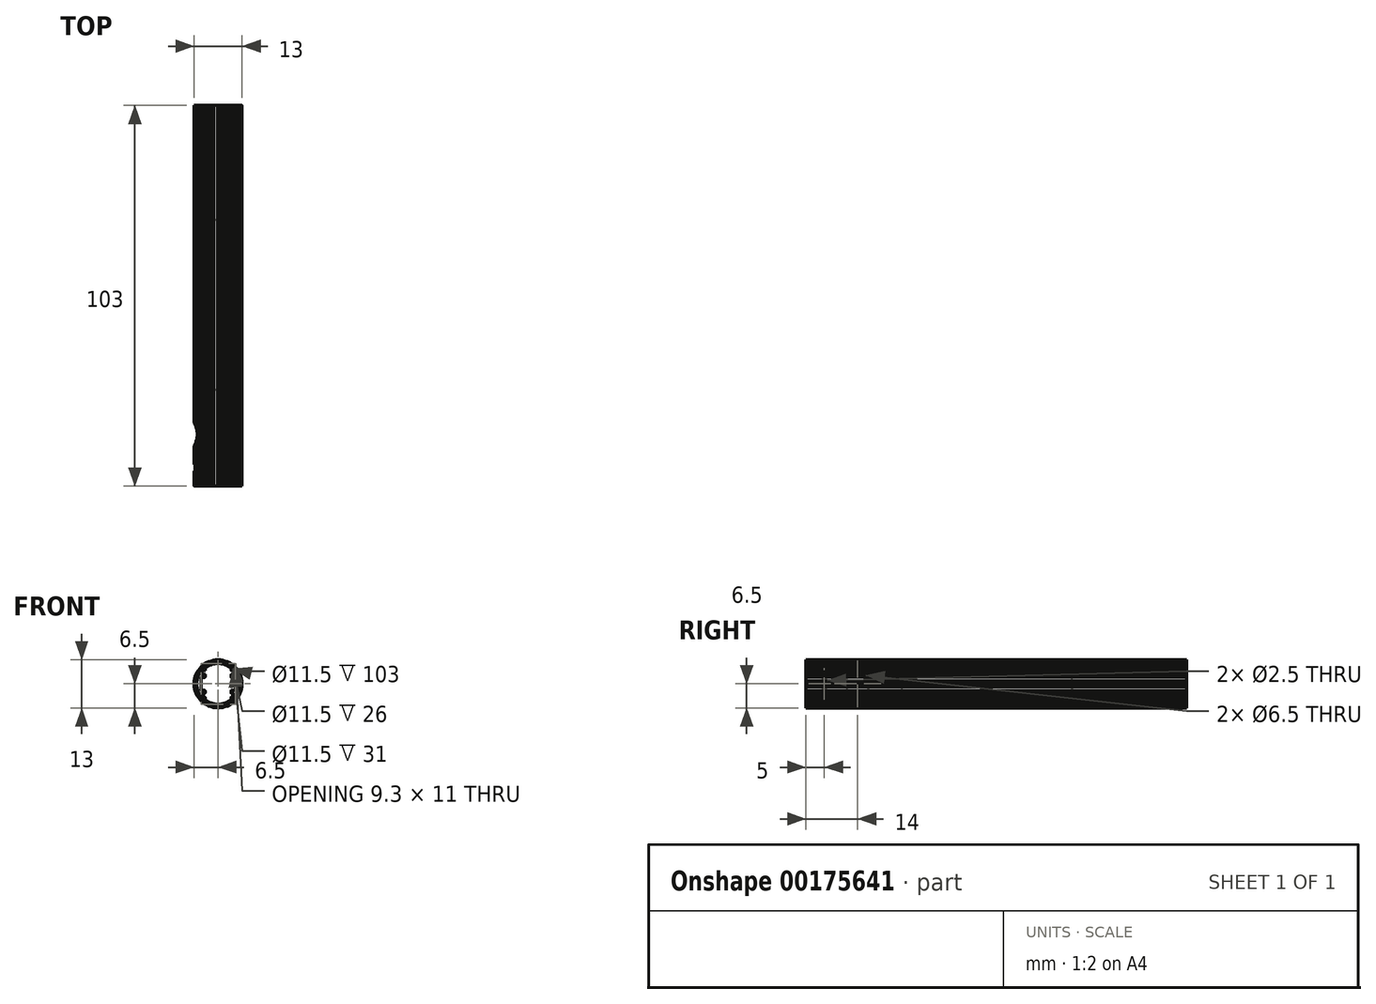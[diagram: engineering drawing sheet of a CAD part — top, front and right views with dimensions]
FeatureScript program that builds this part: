
annotation { "Feature Type Name" : "Feature", "Feature Type Description" : "" }
export const myFeature = defineFeature(function(context is Context, id is Id, definition is map)
    precondition{}
    {
        {
            assignVariable(context, id + "F0", {"name" : "Main_Length", "anyValue" : 103});
        }
        {
            assignVariable(context, id + "F1", {"name" : "Bore_Depth_F", "anyValue" : 26});
        }
        {
            assignVariable(context, id + "F2", {"name" : "Bore_Depth_R", "anyValue" : 31});
        }
        {
            var Q0;
            Q0=qCreatedBy(makeId("Front.planeOp"),FACE);
            var sketch = newSketch(context, id + "F3", { "sketchPlane" : qUnion([Q0])});
            skLineSegment(sketch, "E0", {"start": v(-3.5, -2.5) * mm, "end": v(-3.5, -1.85) * mm});
            skLineSegment(sketch, "E1", {"start": v(6.33, 0.97) * mm, "end": v(6.44, 0.88) * mm});
            skArc(sketch, "E2", {"start": v(-3.6, -1.75) * mm, "mid": v(-3.53, -1.78) * mm, "end": v(-3.5, -1.85) * mm});
            skArc(sketch, "E3", {"start": v(4.25, 3.55) * mm, "mid": v(4.32, 3.52) * mm, "end": v(4.35, 3.45) * mm});
            skArc(sketch, "E4", {"start": v(-3.5, -4.24) * mm, "mid": v(0, -5.5) * mm, "end": v(3.5, -4.24) * mm});
            skLineSegment(sketch, "E5", {"start": v(1.03, 6.32) * mm, "end": v(1.16, 6.4) * mm});
            skLineSegment(sketch, "E6", {"start": v(-4.95, -4.05) * mm, "end": v(-4.96, -4.2) * mm});
            skArc(sketch, "E7", {"start": v(-5.73, -3.08) * mm, "mid": v(-5.63, -3.25) * mm, "end": v(-5.53, -3.42) * mm});
            skLineSegment(sketch, "E8", {"start": v(3.51, 5.35) * mm, "end": v(3.66, 5.37) * mm});
            skLineSegment(sketch, "E9", {"start": v(4.65, -1.65) * mm, "end": v(4.65, 0) * mm});
            skLineSegment(sketch, "E10", {"start": v(-1.63, -6.19) * mm, "end": v(-1.55, -6.31) * mm});
            skArc(sketch, "E11", {"start": v(6.12, -2.2) * mm, "mid": v(6.18, -2) * mm, "end": v(6.24, -1.82) * mm});
            skArc(sketch, "E12", {"start": v(-2.83, -5.85) * mm, "mid": v(-2.64, -5.94) * mm, "end": v(-2.46, -6.02) * mm});
            skArc(sketch, "E13", {"start": v(2.83, 5.85) * mm, "mid": v(2.64, 5.94) * mm, "end": v(2.46, 6.02) * mm});
            skLineSegment(sketch, "E14", {"start": v(4.55, 4.5) * mm, "end": v(4.7, 4.5) * mm});
            skArc(sketch, "E15", {"start": v(-4.35, 2.7) * mm, "mid": v(-4.32, 2.63) * mm, "end": v(-4.25, 2.6) * mm});
            skArc(sketch, "E16", {"start": v(3.98, 5.14) * mm, "mid": v(3.82, 5.26) * mm, "end": v(3.66, 5.37) * mm});
            skLineSegment(sketch, "E17", {"start": v(-6.33, 0.97) * mm, "end": v(-6.44, 0.88) * mm});
            skArc(sketch, "E18", {"start": v(1.16, -6.4) * mm, "mid": v(1.35, -6.36) * mm, "end": v(1.55, -6.31) * mm});
            skLineSegment(sketch, "E19", {"start": v(-4, 5) * mm, "end": v(-3.98, 5.14) * mm});
            skArc(sketch, "E20", {"start": v(-1.55, -6.31) * mm, "mid": v(-1.35, -6.36) * mm, "end": v(-1.16, -6.4) * mm});
            skLineSegment(sketch, "E21", {"start": v(5.38, 3.46) * mm, "end": v(5.53, 3.42) * mm});
            skLineSegment(sketch, "E22", {"start": v(1.63, 6.19) * mm, "end": v(1.55, 6.31) * mm});
            skArc(sketch, "E23", {"start": v(3.5, -2.5) * mm, "mid": v(3.53, -2.57) * mm, "end": v(3.6, -2.6) * mm});
            skLineSegment(sketch, "E24", {"start": v(4, -5) * mm, "end": v(3.98, -5.14) * mm});
            skArc(sketch, "E25", {"start": v(3.6, 1.75) * mm, "mid": v(3.53, 1.78) * mm, "end": v(3.5, 1.85) * mm});
            skArc(sketch, "E26", {"start": v(2.88, -5.72) * mm, "mid": v(3.2, -5.54) * mm, "end": v(3.51, -5.35) * mm});
            skArc(sketch, "E27", {"start": v(-3.6, 3.55) * mm, "mid": v(-3.53, 3.58) * mm, "end": v(-3.5, 3.65) * mm});
            skArc(sketch, "E28", {"start": v(-5.53, 3.42) * mm, "mid": v(-5.63, 3.25) * mm, "end": v(-5.73, 3.08) * mm});
            skLineSegment(sketch, "E29", {"start": v(5.38, -3.46) * mm, "end": v(5.53, -3.42) * mm});
            skArc(sketch, "E30", {"start": v(5.73, 3.08) * mm, "mid": v(5.63, 3.25) * mm, "end": v(5.53, 3.42) * mm});
            skLineSegment(sketch, "E31", {"start": v(-4.25, 2.6) * mm, "end": v(-3.6, 2.6) * mm});
            skLineSegment(sketch, "E32", {"start": v(-3.5, 2.5) * mm, "end": v(-3.5, 1.85) * mm});
            skArc(sketch, "E33", {"start": v(6.24, 1.82) * mm, "mid": v(6.18, 2) * mm, "end": v(6.12, 2.2) * mm});
            skLineSegment(sketch, "E34", {"start": v(4.25, 2.6) * mm, "end": v(3.6, 2.6) * mm});
            skLineSegment(sketch, "E35", {"start": v(2.88, -5.72) * mm, "end": v(2.83, -5.85) * mm});
            skLineSegment(sketch, "E36", {"start": v(3.5, 4.24) * mm, "end": v(3.5, 3.65) * mm});
            skArc(sketch, "E37", {"start": v(5.99, 2.26) * mm, "mid": v(5.85, 2.6) * mm, "end": v(5.69, 2.93) * mm});
            skArc(sketch, "E38", {"start": v(0.3, -6.4) * mm, "mid": v(0.67, -6.36) * mm, "end": v(1.03, -6.32) * mm});
            skArc(sketch, "E39", {"start": v(6.48, 0.48) * mm, "mid": v(6.46, 0.68) * mm, "end": v(6.44, 0.88) * mm});
            skArc(sketch, "E40", {"start": v(-2.88, 5.72) * mm, "mid": v(-3.2, 5.54) * mm, "end": v(-3.51, 5.35) * mm});
            skLineSegment(sketch, "E41", {"start": v(-0.3, 6.4) * mm, "end": v(-0.2, 6.5) * mm});
            skLineSegment(sketch, "E42", {"start": v(5.69, 2.93) * mm, "end": v(5.73, 3.08) * mm});
            skLineSegment(sketch, "E43", {"start": v(1.63, -6.19) * mm, "end": v(1.55, -6.31) * mm});
            skArc(sketch, "E44", {"start": v(-0.3, 6.4) * mm, "mid": v(-0.67, 6.36) * mm, "end": v(-1.03, 6.32) * mm});
            skLineSegment(sketch, "E45", {"start": v(-3.51, 5.35) * mm, "end": v(-3.66, 5.37) * mm});
            skLineSegment(sketch, "E46", {"start": v(-1.63, 6.19) * mm, "end": v(-1.55, 6.31) * mm});
            skLineSegment(sketch, "E47", {"start": v(4.55, -4.5) * mm, "end": v(4.7, -4.5) * mm});
            skArc(sketch, "E48", {"start": v(6.44, -0.88) * mm, "mid": v(6.46, -0.68) * mm, "end": v(6.48, -0.48) * mm});
            skArc(sketch, "E49", {"start": v(-2.46, 6.02) * mm, "mid": v(-2.64, 5.94) * mm, "end": v(-2.83, 5.85) * mm});
            skArc(sketch, "E50", {"start": v(6.33, 0.97) * mm, "mid": v(6.26, 1.33) * mm, "end": v(6.17, 1.69) * mm});
            skArc(sketch, "E51", {"start": v(3.6, 3.55) * mm, "mid": v(3.53, 3.58) * mm, "end": v(3.5, 3.65) * mm});
            skLineSegment(sketch, "E52", {"start": v(3.5, 2.5) * mm, "end": v(3.5, 1.85) * mm});
            skArc(sketch, "E53", {"start": v(-0.2, -6.5) * mm, "mid": v(0, -6.5) * mm, "end": v(0.2, -6.5) * mm});
            skArc(sketch, "E54", {"start": v(4.96, 4.2) * mm, "mid": v(4.83, 4.35) * mm, "end": v(4.7, 4.5) * mm});
            skLineSegment(sketch, "E55", {"start": v(2.32, 5.96) * mm, "end": v(2.46, 6.02) * mm});
            skArc(sketch, "E56", {"start": v(4.35, 2.7) * mm, "mid": v(4.32, 2.63) * mm, "end": v(4.25, 2.6) * mm});
            skLineSegment(sketch, "E57", {"start": v(-4.65, -1.65) * mm, "end": v(-4.65, 0) * mm});
            skArc(sketch, "E58", {"start": v(-1.63, 6.19) * mm, "mid": v(-1.98, 6.09) * mm, "end": v(-2.32, 5.96) * mm});
            skLineSegment(sketch, "E59", {"start": v(-1.03, 6.32) * mm, "end": v(-1.16, 6.4) * mm});
            skLineSegment(sketch, "E60", {"start": v(0.3, -6.4) * mm, "end": v(0.2, -6.5) * mm});
            skArc(sketch, "E61", {"start": v(-4.7, 4.5) * mm, "mid": v(-4.83, 4.35) * mm, "end": v(-4.96, 4.2) * mm});
            skArc(sketch, "E62", {"start": v(-5.69, 2.93) * mm, "mid": v(-5.85, 2.6) * mm, "end": v(-5.99, 2.26) * mm});
            skArc(sketch, "E63", {"start": v(4.25, -3.55) * mm, "mid": v(4.32, -3.52) * mm, "end": v(4.35, -3.45) * mm});
            skLineSegment(sketch, "E64", {"start": v(-4.35, 3.45) * mm, "end": v(-4.35, 2.7) * mm});
            skLineSegment(sketch, "E65", {"start": v(-4.65, 1.65) * mm, "end": v(-4.65, 0) * mm});
            skArc(sketch, "E66", {"start": v(5.69, -2.93) * mm, "mid": v(5.85, -2.6) * mm, "end": v(5.99, -2.26) * mm});
            skArc(sketch, "E67", {"start": v(-4.55, 1.75) * mm, "mid": v(-4.62, 1.72) * mm, "end": v(-4.65, 1.65) * mm});
            skLineSegment(sketch, "E68", {"start": v(-3.5, 4.24) * mm, "end": v(-3.5, 3.65) * mm});
            skLineSegment(sketch, "E69", {"start": v(-3.6, 3.55) * mm, "end": v(-4.25, 3.55) * mm});
            skLineSegment(sketch, "E70", {"start": v(-3.6, 1.75) * mm, "end": v(-4.55, 1.75) * mm});
            skArc(sketch, "E71", {"start": v(-3.5, 2.5) * mm, "mid": v(-3.53, 2.57) * mm, "end": v(-3.6, 2.6) * mm});
            skArc(sketch, "E72", {"start": v(-3.6, 1.75) * mm, "mid": v(-3.53, 1.78) * mm, "end": v(-3.5, 1.85) * mm});
            skArc(sketch, "E73", {"start": v(-4.25, 3.55) * mm, "mid": v(-4.32, 3.52) * mm, "end": v(-4.35, 3.45) * mm});
            skArc(sketch, "E74", {"start": v(4.55, 1.75) * mm, "mid": v(4.62, 1.72) * mm, "end": v(4.65, 1.65) * mm});
            skLineSegment(sketch, "E75", {"start": v(3.6, 1.75) * mm, "end": v(4.55, 1.75) * mm});
            skArc(sketch, "E76", {"start": v(3.5, 2.5) * mm, "mid": v(3.53, 2.57) * mm, "end": v(3.6, 2.6) * mm});
            skArc(sketch, "E77", {"start": v(0.2, 6.5) * mm, "mid": v(0, 6.5) * mm, "end": v(-0.2, 6.5) * mm});
            skLineSegment(sketch, "E78", {"start": v(3.6, 3.55) * mm, "end": v(4.25, 3.55) * mm});
            skLineSegment(sketch, "E79", {"start": v(4.65, 1.65) * mm, "end": v(4.65, 0) * mm});
            skLineSegment(sketch, "E80", {"start": v(4.35, 3.45) * mm, "end": v(4.35, 2.7) * mm});
            skArc(sketch, "E81", {"start": v(-3.6, -3.55) * mm, "mid": v(-3.53, -3.58) * mm, "end": v(-3.5, -3.65) * mm});
            skLineSegment(sketch, "E82", {"start": v(-4.25, -2.6) * mm, "end": v(-3.6, -2.6) * mm});
            skLineSegment(sketch, "E83", {"start": v(-3.6, -1.75) * mm, "end": v(-4.55, -1.75) * mm});
            skArc(sketch, "E84", {"start": v(-3.5, -2.5) * mm, "mid": v(-3.53, -2.57) * mm, "end": v(-3.6, -2.6) * mm});
            skArc(sketch, "E85", {"start": v(-4.55, -1.75) * mm, "mid": v(-4.62, -1.72) * mm, "end": v(-4.65, -1.65) * mm});
            skArc(sketch, "E86", {"start": v(-4.35, -2.7) * mm, "mid": v(-4.32, -2.63) * mm, "end": v(-4.25, -2.6) * mm});
            skArc(sketch, "E87", {"start": v(-4.25, -3.55) * mm, "mid": v(-4.32, -3.52) * mm, "end": v(-4.35, -3.45) * mm});
            skArc(sketch, "E88", {"start": v(3.6, -1.75) * mm, "mid": v(3.53, -1.78) * mm, "end": v(3.5, -1.85) * mm});
            skLineSegment(sketch, "E89", {"start": v(-2.32, 5.96) * mm, "end": v(-2.46, 6.02) * mm});
            skArc(sketch, "E90", {"start": v(4.55, -1.75) * mm, "mid": v(4.62, -1.72) * mm, "end": v(4.65, -1.65) * mm});
            skLineSegment(sketch, "E91", {"start": v(3.6, -1.75) * mm, "end": v(4.55, -1.75) * mm});
            skArc(sketch, "E92", {"start": v(4.35, -2.7) * mm, "mid": v(4.32, -2.63) * mm, "end": v(4.25, -2.6) * mm});
            skLineSegment(sketch, "E93", {"start": v(4.25, -2.6) * mm, "end": v(3.6, -2.6) * mm});
            skArc(sketch, "E94", {"start": v(3.6, -3.55) * mm, "mid": v(3.53, -3.58) * mm, "end": v(3.5, -3.65) * mm});
            skLineSegment(sketch, "E95", {"start": v(-3.5, -4.24) * mm, "end": v(-3.5, -3.65) * mm});
            skLineSegment(sketch, "E96", {"start": v(3.5, -2.5) * mm, "end": v(3.5, -1.85) * mm});
            skLineSegment(sketch, "E97", {"start": v(4.35, -3.45) * mm, "end": v(4.35, -2.7) * mm});
            skLineSegment(sketch, "E98", {"start": v(-3.6, -3.55) * mm, "end": v(-4.25, -3.55) * mm});
            skArc(sketch, "E99", {"start": v(-6.12, 2.2) * mm, "mid": v(-6.18, 2) * mm, "end": v(-6.24, 1.82) * mm});
            skLineSegment(sketch, "E100", {"start": v(-4.35, -3.45) * mm, "end": v(-4.35, -2.7) * mm});
            skLineSegment(sketch, "E101", {"start": v(3.6, -3.55) * mm, "end": v(4.25, -3.55) * mm});
            skLineSegment(sketch, "E102", {"start": v(-5.38, 3.46) * mm, "end": v(-5.53, 3.42) * mm});
            skLineSegment(sketch, "E103", {"start": v(3.5, -4.24) * mm, "end": v(3.5, -3.65) * mm});
            skArc(sketch, "E104", {"start": v(3.5, 4.24) * mm, "mid": v(0, 5.5) * mm, "end": v(-3.5, 4.24) * mm});
            skLineSegment(sketch, "E105", {"start": v(-0.3, -6.4) * mm, "end": v(-0.2, -6.5) * mm});
            skArc(sketch, "E106", {"start": v(1.63, -6.19) * mm, "mid": v(1.98, -6.09) * mm, "end": v(2.32, -5.96) * mm});
            skLineSegment(sketch, "E107", {"start": v(1.03, -6.32) * mm, "end": v(1.16, -6.4) * mm});
            skArc(sketch, "E108", {"start": v(2.46, -6.02) * mm, "mid": v(2.64, -5.94) * mm, "end": v(2.83, -5.85) * mm});
            skArc(sketch, "E109", {"start": v(-6.24, -1.82) * mm, "mid": v(-6.18, -2) * mm, "end": v(-6.12, -2.2) * mm});
            skLineSegment(sketch, "E110", {"start": v(2.32, -5.96) * mm, "end": v(2.46, -6.02) * mm});
            skArc(sketch, "E111", {"start": v(4, -5) * mm, "mid": v(4.28, -4.76) * mm, "end": v(4.55, -4.5) * mm});
            skArc(sketch, "E112", {"start": v(3.66, -5.37) * mm, "mid": v(3.82, -5.26) * mm, "end": v(3.98, -5.14) * mm});
            skLineSegment(sketch, "E113", {"start": v(3.51, -5.35) * mm, "end": v(3.66, -5.37) * mm});
            skLineSegment(sketch, "E114", {"start": v(-3.51, -5.35) * mm, "end": v(-3.66, -5.37) * mm});
            skLineSegment(sketch, "E115", {"start": v(4.95, -4.05) * mm, "end": v(4.96, -4.2) * mm});
            skLineSegment(sketch, "E116", {"start": v(-4.55, -4.5) * mm, "end": v(-4.7, -4.5) * mm});
            skArc(sketch, "E117", {"start": v(5.53, -3.42) * mm, "mid": v(5.63, -3.25) * mm, "end": v(5.73, -3.08) * mm});
            skArc(sketch, "E118", {"start": v(4.7, -4.5) * mm, "mid": v(4.83, -4.35) * mm, "end": v(4.96, -4.2) * mm});
            skArc(sketch, "E119", {"start": v(-3.98, -5.14) * mm, "mid": v(-3.82, -5.26) * mm, "end": v(-3.66, -5.37) * mm});
            skArc(sketch, "E120", {"start": v(6.17, -1.69) * mm, "mid": v(6.26, -1.33) * mm, "end": v(6.33, -0.97) * mm});
            skLineSegment(sketch, "E121", {"start": v(6.17, -1.69) * mm, "end": v(6.24, -1.82) * mm});
            skLineSegment(sketch, "E122", {"start": v(5.99, -2.26) * mm, "end": v(6.12, -2.2) * mm});
            skArc(sketch, "E123", {"start": v(6.39, -0.37) * mm, "mid": v(6.4, 0) * mm, "end": v(6.39, 0.37) * mm});
            skLineSegment(sketch, "E124", {"start": v(6.39, -0.37) * mm, "end": v(6.48, -0.48) * mm});
            skLineSegment(sketch, "E125", {"start": v(-1.03, -6.32) * mm, "end": v(-1.16, -6.4) * mm});
            skLineSegment(sketch, "E126", {"start": v(6.33, -0.97) * mm, "end": v(6.44, -0.88) * mm});
            skLineSegment(sketch, "E127", {"start": v(5.99, 2.26) * mm, "end": v(6.12, 2.2) * mm});
            skLineSegment(sketch, "E128", {"start": v(6.17, 1.69) * mm, "end": v(6.24, 1.82) * mm});
            skArc(sketch, "E129", {"start": v(5.38, 3.46) * mm, "mid": v(5.18, 3.76) * mm, "end": v(4.95, 4.05) * mm});
            skArc(sketch, "E130", {"start": v(4.55, 4.5) * mm, "mid": v(4.28, 4.76) * mm, "end": v(4, 5) * mm});
            skLineSegment(sketch, "E131", {"start": v(4.95, 4.05) * mm, "end": v(4.96, 4.2) * mm});
            skArc(sketch, "E132", {"start": v(3.51, 5.35) * mm, "mid": v(3.2, 5.54) * mm, "end": v(2.88, 5.72) * mm});
            skLineSegment(sketch, "E133", {"start": v(4, 5) * mm, "end": v(3.98, 5.14) * mm});
            skArc(sketch, "E134", {"start": v(2.32, 5.96) * mm, "mid": v(1.98, 6.09) * mm, "end": v(1.63, 6.19) * mm});
            skLineSegment(sketch, "E135", {"start": v(2.88, 5.72) * mm, "end": v(2.83, 5.85) * mm});
            skArc(sketch, "E136", {"start": v(1.03, 6.32) * mm, "mid": v(0.67, 6.36) * mm, "end": v(0.3, 6.4) * mm});
            skArc(sketch, "E137", {"start": v(1.55, 6.31) * mm, "mid": v(1.35, 6.36) * mm, "end": v(1.16, 6.4) * mm});
            skLineSegment(sketch, "E138", {"start": v(0.3, 6.4) * mm, "end": v(0.2, 6.5) * mm});
            skArc(sketch, "E139", {"start": v(-1.16, 6.4) * mm, "mid": v(-1.35, 6.36) * mm, "end": v(-1.55, 6.31) * mm});
            skLineSegment(sketch, "E140", {"start": v(-2.88, 5.72) * mm, "end": v(-2.83, 5.85) * mm});
            skArc(sketch, "E141", {"start": v(-4, 5) * mm, "mid": v(-4.28, 4.76) * mm, "end": v(-4.55, 4.5) * mm});
            skArc(sketch, "E142", {"start": v(-3.66, 5.37) * mm, "mid": v(-3.82, 5.26) * mm, "end": v(-3.98, 5.14) * mm});
            skLineSegment(sketch, "E143", {"start": v(-6.33, -0.97) * mm, "end": v(-6.44, -0.88) * mm});
            skLineSegment(sketch, "E144", {"start": v(-4.95, 4.05) * mm, "end": v(-4.96, 4.2) * mm});
            skLineSegment(sketch, "E145", {"start": v(-4.55, 4.5) * mm, "end": v(-4.7, 4.5) * mm});
            skArc(sketch, "E146", {"start": v(-6.17, 1.69) * mm, "mid": v(-6.26, 1.33) * mm, "end": v(-6.33, 0.97) * mm});
            skLineSegment(sketch, "E147", {"start": v(-6.17, 1.69) * mm, "end": v(-6.24, 1.82) * mm});
            skLineSegment(sketch, "E148", {"start": v(-5.99, 2.26) * mm, "end": v(-6.12, 2.2) * mm});
            skArc(sketch, "E149", {"start": v(-6.39, 0.37) * mm, "mid": v(-6.4, 0) * mm, "end": v(-6.39, -0.37) * mm});
            skArc(sketch, "E150", {"start": v(-6.44, 0.88) * mm, "mid": v(-6.46, 0.68) * mm, "end": v(-6.48, 0.48) * mm});
            skLineSegment(sketch, "E151", {"start": v(-6.39, 0.37) * mm, "end": v(-6.48, 0.48) * mm});
            skLineSegment(sketch, "E152", {"start": v(5.69, -2.93) * mm, "end": v(5.73, -3.08) * mm});
            skArc(sketch, "E153", {"start": v(-6.33, -0.97) * mm, "mid": v(-6.26, -1.33) * mm, "end": v(-6.17, -1.69) * mm});
            skArc(sketch, "E154", {"start": v(-6.48, -0.48) * mm, "mid": v(-6.46, -0.68) * mm, "end": v(-6.44, -0.88) * mm});
            skLineSegment(sketch, "E155", {"start": v(-6.39, -0.37) * mm, "end": v(-6.48, -0.48) * mm});
            skArc(sketch, "E156", {"start": v(-5.99, -2.26) * mm, "mid": v(-5.85, -2.6) * mm, "end": v(-5.69, -2.93) * mm});
            skLineSegment(sketch, "E157", {"start": v(-5.99, -2.26) * mm, "end": v(-6.12, -2.2) * mm});
            skLineSegment(sketch, "E158", {"start": v(-6.17, -1.69) * mm, "end": v(-6.24, -1.82) * mm});
            skArc(sketch, "E159", {"start": v(-5.38, -3.46) * mm, "mid": v(-5.18, -3.76) * mm, "end": v(-4.95, -4.05) * mm});
            skLineSegment(sketch, "E160", {"start": v(-5.38, -3.46) * mm, "end": v(-5.53, -3.42) * mm});
            skLineSegment(sketch, "E161", {"start": v(-5.69, -2.93) * mm, "end": v(-5.73, -3.08) * mm});
            skArc(sketch, "E162", {"start": v(-4.55, -4.5) * mm, "mid": v(-4.28, -4.76) * mm, "end": v(-4, -5) * mm});
            skLineSegment(sketch, "E163", {"start": v(6.39, 0.37) * mm, "end": v(6.48, 0.48) * mm});
            skArc(sketch, "E164", {"start": v(-4.96, -4.2) * mm, "mid": v(-4.83, -4.35) * mm, "end": v(-4.7, -4.5) * mm});
            skArc(sketch, "E165", {"start": v(4.95, -4.05) * mm, "mid": v(5.18, -3.76) * mm, "end": v(5.38, -3.46) * mm});
            skLineSegment(sketch, "E166", {"start": v(-4, -5) * mm, "end": v(-3.98, -5.14) * mm});
            skArc(sketch, "E167", {"start": v(-2.32, -5.96) * mm, "mid": v(-1.98, -6.09) * mm, "end": v(-1.63, -6.19) * mm});
            skLineSegment(sketch, "E168", {"start": v(-2.32, -5.96) * mm, "end": v(-2.46, -6.02) * mm});
            skLineSegment(sketch, "E169", {"start": v(-2.88, -5.72) * mm, "end": v(-2.83, -5.85) * mm});
            skArc(sketch, "E170", {"start": v(-1.03, -6.32) * mm, "mid": v(-0.67, -6.36) * mm, "end": v(-0.3, -6.4) * mm});
            skArc(sketch, "E171", {"start": v(-4.95, 4.05) * mm, "mid": v(-5.18, 3.76) * mm, "end": v(-5.38, 3.46) * mm});
            skLineSegment(sketch, "E172", {"start": v(-5.69, 2.93) * mm, "end": v(-5.73, 3.08) * mm});
            skArc(sketch, "E173", {"start": v(-3.51, -5.35) * mm, "mid": v(-3.2, -5.54) * mm, "end": v(-2.88, -5.72) * mm});
            skSolve(sketch);
        }
        {
            var Q0;
            Q0=makeQuery(id+"F3.imprint","IMPRINT",FACE,{"disambiguationData":[TD([[makeQuery(id+"F3.imprint","IMPRINT",EDGE,{"derivedFrom":sQuery(id+"F3.wireOp",EDGE,"E0")}),1.0]])]});
            extrude(context, id + "F4", {"entities" : qUnion([Q0]), "depth" : (getVariable(context, 'Main_Length') - getVariable(context, 'Bore_Depth_F') - getVariable(context, 'Bore_Depth_R')) * mm});
        }
        {
            var Q0;
            Q0=makeQuery(id+"F4.opExtrude","CAP_FACE",FACE,{"disambiguationData":[OSD([sQuery(id+"F3.wireOp",EDGE,"E0"),sQuery(id+"F3.wireOp",EDGE,"E1"),sQuery(id+"F3.wireOp",EDGE,"E2"),sQuery(id+"F3.wireOp",EDGE,"E3"),sQuery(id+"F3.wireOp",EDGE,"E4"),sQuery(id+"F3.wireOp",EDGE,"E5"),sQuery(id+"F3.wireOp",EDGE,"E6"),sQuery(id+"F3.wireOp",EDGE,"E7"),sQuery(id+"F3.wireOp",EDGE,"E8"),sQuery(id+"F3.wireOp",EDGE,"E9"),sQuery(id+"F3.wireOp",EDGE,"E10"),sQuery(id+"F3.wireOp",EDGE,"E11"),sQuery(id+"F3.wireOp",EDGE,"E12"),sQuery(id+"F3.wireOp",EDGE,"E13"),sQuery(id+"F3.wireOp",EDGE,"E14"),sQuery(id+"F3.wireOp",EDGE,"E15"),sQuery(id+"F3.wireOp",EDGE,"E16"),sQuery(id+"F3.wireOp",EDGE,"E17"),sQuery(id+"F3.wireOp",EDGE,"E18"),sQuery(id+"F3.wireOp",EDGE,"E19"),sQuery(id+"F3.wireOp",EDGE,"E20"),sQuery(id+"F3.wireOp",EDGE,"E21"),sQuery(id+"F3.wireOp",EDGE,"E22"),sQuery(id+"F3.wireOp",EDGE,"E23"),sQuery(id+"F3.wireOp",EDGE,"E24"),sQuery(id+"F3.wireOp",EDGE,"E25"),sQuery(id+"F3.wireOp",EDGE,"E26"),sQuery(id+"F3.wireOp",EDGE,"E27"),sQuery(id+"F3.wireOp",EDGE,"E28"),sQuery(id+"F3.wireOp",EDGE,"E29"),sQuery(id+"F3.wireOp",EDGE,"E30"),sQuery(id+"F3.wireOp",EDGE,"E31"),sQuery(id+"F3.wireOp",EDGE,"E32"),sQuery(id+"F3.wireOp",EDGE,"E33"),sQuery(id+"F3.wireOp",EDGE,"E34"),sQuery(id+"F3.wireOp",EDGE,"E35"),sQuery(id+"F3.wireOp",EDGE,"E36"),sQuery(id+"F3.wireOp",EDGE,"E37"),sQuery(id+"F3.wireOp",EDGE,"E38"),sQuery(id+"F3.wireOp",EDGE,"E39"),sQuery(id+"F3.wireOp",EDGE,"E40"),sQuery(id+"F3.wireOp",EDGE,"E41"),sQuery(id+"F3.wireOp",EDGE,"E42"),sQuery(id+"F3.wireOp",EDGE,"E43"),sQuery(id+"F3.wireOp",EDGE,"E44"),sQuery(id+"F3.wireOp",EDGE,"E45"),sQuery(id+"F3.wireOp",EDGE,"E46"),sQuery(id+"F3.wireOp",EDGE,"E47"),sQuery(id+"F3.wireOp",EDGE,"E48"),sQuery(id+"F3.wireOp",EDGE,"E49"),sQuery(id+"F3.wireOp",EDGE,"E50"),sQuery(id+"F3.wireOp",EDGE,"E51"),sQuery(id+"F3.wireOp",EDGE,"E52"),sQuery(id+"F3.wireOp",EDGE,"E53"),sQuery(id+"F3.wireOp",EDGE,"E54"),sQuery(id+"F3.wireOp",EDGE,"E55"),sQuery(id+"F3.wireOp",EDGE,"E56"),sQuery(id+"F3.wireOp",EDGE,"E57"),sQuery(id+"F3.wireOp",EDGE,"E58"),sQuery(id+"F3.wireOp",EDGE,"E59"),sQuery(id+"F3.wireOp",EDGE,"E60"),sQuery(id+"F3.wireOp",EDGE,"E61"),sQuery(id+"F3.wireOp",EDGE,"E62"),sQuery(id+"F3.wireOp",EDGE,"E63"),sQuery(id+"F3.wireOp",EDGE,"E64"),sQuery(id+"F3.wireOp",EDGE,"E65"),sQuery(id+"F3.wireOp",EDGE,"E66"),sQuery(id+"F3.wireOp",EDGE,"E67"),sQuery(id+"F3.wireOp",EDGE,"E68"),sQuery(id+"F3.wireOp",EDGE,"E69"),sQuery(id+"F3.wireOp",EDGE,"E70"),sQuery(id+"F3.wireOp",EDGE,"E71"),sQuery(id+"F3.wireOp",EDGE,"E72"),sQuery(id+"F3.wireOp",EDGE,"E73"),sQuery(id+"F3.wireOp",EDGE,"E74"),sQuery(id+"F3.wireOp",EDGE,"E75"),sQuery(id+"F3.wireOp",EDGE,"E76"),sQuery(id+"F3.wireOp",EDGE,"E77"),sQuery(id+"F3.wireOp",EDGE,"E78"),sQuery(id+"F3.wireOp",EDGE,"E79"),sQuery(id+"F3.wireOp",EDGE,"E80"),sQuery(id+"F3.wireOp",EDGE,"E81"),sQuery(id+"F3.wireOp",EDGE,"E82"),sQuery(id+"F3.wireOp",EDGE,"E83"),sQuery(id+"F3.wireOp",EDGE,"E84"),sQuery(id+"F3.wireOp",EDGE,"E85"),sQuery(id+"F3.wireOp",EDGE,"E86"),sQuery(id+"F3.wireOp",EDGE,"E87"),sQuery(id+"F3.wireOp",EDGE,"E88"),sQuery(id+"F3.wireOp",EDGE,"E89"),sQuery(id+"F3.wireOp",EDGE,"E90"),sQuery(id+"F3.wireOp",EDGE,"E91"),sQuery(id+"F3.wireOp",EDGE,"E92"),sQuery(id+"F3.wireOp",EDGE,"E93"),sQuery(id+"F3.wireOp",EDGE,"E94"),sQuery(id+"F3.wireOp",EDGE,"E95"),sQuery(id+"F3.wireOp",EDGE,"E96"),sQuery(id+"F3.wireOp",EDGE,"E97"),sQuery(id+"F3.wireOp",EDGE,"E98"),sQuery(id+"F3.wireOp",EDGE,"E99"),sQuery(id+"F3.wireOp",EDGE,"E100"),sQuery(id+"F3.wireOp",EDGE,"E101"),sQuery(id+"F3.wireOp",EDGE,"E102"),sQuery(id+"F3.wireOp",EDGE,"E103"),sQuery(id+"F3.wireOp",EDGE,"E104"),sQuery(id+"F3.wireOp",EDGE,"E105"),sQuery(id+"F3.wireOp",EDGE,"E106"),sQuery(id+"F3.wireOp",EDGE,"E107"),sQuery(id+"F3.wireOp",EDGE,"E108"),sQuery(id+"F3.wireOp",EDGE,"E109"),sQuery(id+"F3.wireOp",EDGE,"E110"),sQuery(id+"F3.wireOp",EDGE,"E111"),sQuery(id+"F3.wireOp",EDGE,"E112"),sQuery(id+"F3.wireOp",EDGE,"E113"),sQuery(id+"F3.wireOp",EDGE,"E114"),sQuery(id+"F3.wireOp",EDGE,"E115"),sQuery(id+"F3.wireOp",EDGE,"E116"),sQuery(id+"F3.wireOp",EDGE,"E117"),sQuery(id+"F3.wireOp",EDGE,"E118"),sQuery(id+"F3.wireOp",EDGE,"E119"),sQuery(id+"F3.wireOp",EDGE,"E120"),sQuery(id+"F3.wireOp",EDGE,"E121"),sQuery(id+"F3.wireOp",EDGE,"E122"),sQuery(id+"F3.wireOp",EDGE,"E123"),sQuery(id+"F3.wireOp",EDGE,"E124"),sQuery(id+"F3.wireOp",EDGE,"E125"),sQuery(id+"F3.wireOp",EDGE,"E126"),sQuery(id+"F3.wireOp",EDGE,"E127"),sQuery(id+"F3.wireOp",EDGE,"E128"),sQuery(id+"F3.wireOp",EDGE,"E129"),sQuery(id+"F3.wireOp",EDGE,"E130"),sQuery(id+"F3.wireOp",EDGE,"E131"),sQuery(id+"F3.wireOp",EDGE,"E132"),sQuery(id+"F3.wireOp",EDGE,"E133"),sQuery(id+"F3.wireOp",EDGE,"E134"),sQuery(id+"F3.wireOp",EDGE,"E135"),sQuery(id+"F3.wireOp",EDGE,"E136"),sQuery(id+"F3.wireOp",EDGE,"E137"),sQuery(id+"F3.wireOp",EDGE,"E138"),sQuery(id+"F3.wireOp",EDGE,"E139"),sQuery(id+"F3.wireOp",EDGE,"E140"),sQuery(id+"F3.wireOp",EDGE,"E141"),sQuery(id+"F3.wireOp",EDGE,"E142"),sQuery(id+"F3.wireOp",EDGE,"E143"),sQuery(id+"F3.wireOp",EDGE,"E144"),sQuery(id+"F3.wireOp",EDGE,"E145"),sQuery(id+"F3.wireOp",EDGE,"E146"),sQuery(id+"F3.wireOp",EDGE,"E147"),sQuery(id+"F3.wireOp",EDGE,"E148"),sQuery(id+"F3.wireOp",EDGE,"E149"),sQuery(id+"F3.wireOp",EDGE,"E150"),sQuery(id+"F3.wireOp",EDGE,"E151"),sQuery(id+"F3.wireOp",EDGE,"E152"),sQuery(id+"F3.wireOp",EDGE,"E153"),sQuery(id+"F3.wireOp",EDGE,"E154"),sQuery(id+"F3.wireOp",EDGE,"E155"),sQuery(id+"F3.wireOp",EDGE,"E156"),sQuery(id+"F3.wireOp",EDGE,"E157"),sQuery(id+"F3.wireOp",EDGE,"E158"),sQuery(id+"F3.wireOp",EDGE,"E159"),sQuery(id+"F3.wireOp",EDGE,"E160"),sQuery(id+"F3.wireOp",EDGE,"E161"),sQuery(id+"F3.wireOp",EDGE,"E162"),sQuery(id+"F3.wireOp",EDGE,"E163"),sQuery(id+"F3.wireOp",EDGE,"E164"),sQuery(id+"F3.wireOp",EDGE,"E165"),sQuery(id+"F3.wireOp",EDGE,"E166"),sQuery(id+"F3.wireOp",EDGE,"E167"),sQuery(id+"F3.wireOp",EDGE,"E168"),sQuery(id+"F3.wireOp",EDGE,"E169"),sQuery(id+"F3.wireOp",EDGE,"E170"),sQuery(id+"F3.wireOp",EDGE,"E171"),sQuery(id+"F3.wireOp",EDGE,"E172"),sQuery(id+"F3.wireOp",EDGE,"E173")])],"isStart":false});
            var sketch = newSketch(context, id + "F5", { "sketchPlane" : qUnion([Q0])});
            skCircle(sketch, "E174", {"center": v(0, 0) * mm, "radius": 5.75 * mm});
            skLineSegment(sketch, "E175.0.0", {"start": v(6.44, 0.88) * mm, "end": v(6.33, 0.97) * mm});
            skArc(sketch, "E175.0.1", {"start": v(6.33, 0.97) * mm, "mid": v(6.26, 1.33) * mm, "end": v(6.17, 1.69) * mm});
            skLineSegment(sketch, "E175.0.2", {"start": v(6.17, 1.69) * mm, "end": v(6.24, 1.82) * mm});
            skArc(sketch, "E175.0.3", {"start": v(6.24, 1.82) * mm, "mid": v(6.18, 2) * mm, "end": v(6.12, 2.2) * mm});
            skLineSegment(sketch, "E175.0.4", {"start": v(6.12, 2.2) * mm, "end": v(5.99, 2.26) * mm});
            skArc(sketch, "E175.0.5", {"start": v(5.99, 2.26) * mm, "mid": v(5.85, 2.6) * mm, "end": v(5.69, 2.93) * mm});
            skLineSegment(sketch, "E175.0.6", {"start": v(5.69, 2.93) * mm, "end": v(5.73, 3.08) * mm});
            skArc(sketch, "E175.0.7", {"start": v(5.73, 3.08) * mm, "mid": v(5.63, 3.25) * mm, "end": v(5.53, 3.42) * mm});
            skLineSegment(sketch, "E175.0.8", {"start": v(5.53, 3.42) * mm, "end": v(5.38, 3.46) * mm});
            skArc(sketch, "E175.0.9", {"start": v(5.38, 3.46) * mm, "mid": v(5.18, 3.76) * mm, "end": v(4.95, 4.05) * mm});
            skLineSegment(sketch, "E175.0.10", {"start": v(4.95, 4.05) * mm, "end": v(4.96, 4.2) * mm});
            skArc(sketch, "E175.0.11", {"start": v(4.96, 4.2) * mm, "mid": v(4.83, 4.35) * mm, "end": v(4.7, 4.5) * mm});
            skLineSegment(sketch, "E175.0.12", {"start": v(4.7, 4.5) * mm, "end": v(4.55, 4.5) * mm});
            skArc(sketch, "E175.0.13", {"start": v(4.55, 4.5) * mm, "mid": v(4.28, 4.76) * mm, "end": v(4, 5) * mm});
            skLineSegment(sketch, "E175.0.14", {"start": v(4, 5) * mm, "end": v(3.98, 5.14) * mm});
            skArc(sketch, "E175.0.15", {"start": v(3.98, 5.14) * mm, "mid": v(3.82, 5.26) * mm, "end": v(3.66, 5.37) * mm});
            skLineSegment(sketch, "E175.0.16", {"start": v(3.66, 5.37) * mm, "end": v(3.51, 5.35) * mm});
            skArc(sketch, "E175.0.17", {"start": v(3.51, 5.35) * mm, "mid": v(3.2, 5.54) * mm, "end": v(2.88, 5.72) * mm});
            skLineSegment(sketch, "E175.0.18", {"start": v(2.88, 5.72) * mm, "end": v(2.83, 5.85) * mm});
            skArc(sketch, "E175.0.19", {"start": v(2.83, 5.85) * mm, "mid": v(2.64, 5.94) * mm, "end": v(2.46, 6.02) * mm});
            skLineSegment(sketch, "E175.0.20", {"start": v(2.46, 6.02) * mm, "end": v(2.32, 5.96) * mm});
            skArc(sketch, "E175.0.21", {"start": v(2.32, 5.96) * mm, "mid": v(1.98, 6.09) * mm, "end": v(1.63, 6.19) * mm});
            skLineSegment(sketch, "E175.0.22", {"start": v(1.63, 6.19) * mm, "end": v(1.55, 6.31) * mm});
            skArc(sketch, "E175.0.23", {"start": v(1.55, 6.31) * mm, "mid": v(1.35, 6.36) * mm, "end": v(1.16, 6.4) * mm});
            skLineSegment(sketch, "E175.0.24", {"start": v(1.16, 6.4) * mm, "end": v(1.03, 6.32) * mm});
            skArc(sketch, "E175.0.25", {"start": v(1.03, 6.32) * mm, "mid": v(0.67, 6.36) * mm, "end": v(0.3, 6.4) * mm});
            skLineSegment(sketch, "E175.0.26", {"start": v(0.3, 6.4) * mm, "end": v(0.2, 6.5) * mm});
            skArc(sketch, "E175.0.27", {"start": v(0.2, 6.5) * mm, "mid": v(0, 6.5) * mm, "end": v(-0.2, 6.5) * mm});
            skLineSegment(sketch, "E175.0.28", {"start": v(-0.2, 6.5) * mm, "end": v(-0.3, 6.4) * mm});
            skArc(sketch, "E175.0.29", {"start": v(-0.3, 6.4) * mm, "mid": v(-0.67, 6.36) * mm, "end": v(-1.03, 6.32) * mm});
            skLineSegment(sketch, "E175.0.30", {"start": v(-1.03, 6.32) * mm, "end": v(-1.16, 6.4) * mm});
            skArc(sketch, "E175.0.31", {"start": v(-1.16, 6.4) * mm, "mid": v(-1.35, 6.36) * mm, "end": v(-1.55, 6.31) * mm});
            skLineSegment(sketch, "E175.0.32", {"start": v(-1.55, 6.31) * mm, "end": v(-1.63, 6.19) * mm});
            skArc(sketch, "E175.0.33", {"start": v(-1.63, 6.19) * mm, "mid": v(-1.98, 6.09) * mm, "end": v(-2.32, 5.96) * mm});
            skLineSegment(sketch, "E175.0.34", {"start": v(-2.32, 5.96) * mm, "end": v(-2.46, 6.02) * mm});
            skArc(sketch, "E175.0.35", {"start": v(-2.46, 6.02) * mm, "mid": v(-2.64, 5.94) * mm, "end": v(-2.83, 5.85) * mm});
            skLineSegment(sketch, "E175.0.36", {"start": v(-2.83, 5.85) * mm, "end": v(-2.88, 5.72) * mm});
            skArc(sketch, "E175.0.37", {"start": v(-2.88, 5.72) * mm, "mid": v(-3.2, 5.54) * mm, "end": v(-3.51, 5.35) * mm});
            skLineSegment(sketch, "E175.0.38", {"start": v(-3.51, 5.35) * mm, "end": v(-3.66, 5.37) * mm});
            skArc(sketch, "E175.0.39", {"start": v(-3.66, 5.37) * mm, "mid": v(-3.82, 5.26) * mm, "end": v(-3.98, 5.14) * mm});
            skLineSegment(sketch, "E175.0.40", {"start": v(-3.98, 5.14) * mm, "end": v(-4, 5) * mm});
            skArc(sketch, "E175.0.41", {"start": v(-4, 5) * mm, "mid": v(-4.28, 4.76) * mm, "end": v(-4.55, 4.5) * mm});
            skLineSegment(sketch, "E175.0.42", {"start": v(-4.55, 4.5) * mm, "end": v(-4.7, 4.5) * mm});
            skArc(sketch, "E175.0.43", {"start": v(-4.7, 4.5) * mm, "mid": v(-4.83, 4.35) * mm, "end": v(-4.96, 4.2) * mm});
            skLineSegment(sketch, "E175.0.44", {"start": v(-4.96, 4.2) * mm, "end": v(-4.95, 4.05) * mm});
            skArc(sketch, "E175.0.45", {"start": v(-4.95, 4.05) * mm, "mid": v(-5.18, 3.76) * mm, "end": v(-5.38, 3.46) * mm});
            skLineSegment(sketch, "E175.0.46", {"start": v(-5.38, 3.46) * mm, "end": v(-5.53, 3.42) * mm});
            skArc(sketch, "E175.0.47", {"start": v(-5.53, 3.42) * mm, "mid": v(-5.63, 3.25) * mm, "end": v(-5.73, 3.08) * mm});
            skLineSegment(sketch, "E175.0.48", {"start": v(-5.73, 3.08) * mm, "end": v(-5.69, 2.93) * mm});
            skArc(sketch, "E175.0.49", {"start": v(-5.69, 2.93) * mm, "mid": v(-5.85, 2.6) * mm, "end": v(-5.99, 2.26) * mm});
            skLineSegment(sketch, "E175.0.50", {"start": v(-5.99, 2.26) * mm, "end": v(-6.12, 2.2) * mm});
            skArc(sketch, "E175.0.51", {"start": v(-6.12, 2.2) * mm, "mid": v(-6.18, 2) * mm, "end": v(-6.24, 1.82) * mm});
            skLineSegment(sketch, "E175.0.52", {"start": v(-6.24, 1.82) * mm, "end": v(-6.17, 1.69) * mm});
            skArc(sketch, "E175.0.53", {"start": v(-6.17, 1.69) * mm, "mid": v(-6.26, 1.33) * mm, "end": v(-6.33, 0.97) * mm});
            skLineSegment(sketch, "E175.0.54", {"start": v(-6.33, 0.97) * mm, "end": v(-6.44, 0.88) * mm});
            skArc(sketch, "E175.0.55", {"start": v(-6.44, 0.88) * mm, "mid": v(-6.46, 0.68) * mm, "end": v(-6.48, 0.48) * mm});
            skLineSegment(sketch, "E175.0.56", {"start": v(-6.48, 0.48) * mm, "end": v(-6.39, 0.37) * mm});
            skArc(sketch, "E175.0.57", {"start": v(-6.39, 0.37) * mm, "mid": v(-6.4, 0) * mm, "end": v(-6.39, -0.37) * mm});
            skLineSegment(sketch, "E175.0.58", {"start": v(-6.39, -0.37) * mm, "end": v(-6.48, -0.48) * mm});
            skArc(sketch, "E175.0.59", {"start": v(-6.48, -0.48) * mm, "mid": v(-6.46, -0.68) * mm, "end": v(-6.44, -0.88) * mm});
            skLineSegment(sketch, "E175.0.60", {"start": v(-6.44, -0.88) * mm, "end": v(-6.33, -0.97) * mm});
            skArc(sketch, "E175.0.61", {"start": v(-6.33, -0.97) * mm, "mid": v(-6.26, -1.33) * mm, "end": v(-6.17, -1.69) * mm});
            skLineSegment(sketch, "E175.0.62", {"start": v(-6.17, -1.69) * mm, "end": v(-6.24, -1.82) * mm});
            skArc(sketch, "E175.0.63", {"start": v(-6.24, -1.82) * mm, "mid": v(-6.18, -2) * mm, "end": v(-6.12, -2.2) * mm});
            skLineSegment(sketch, "E175.0.64", {"start": v(-6.12, -2.2) * mm, "end": v(-5.99, -2.26) * mm});
            skArc(sketch, "E175.0.65", {"start": v(-5.99, -2.26) * mm, "mid": v(-5.85, -2.6) * mm, "end": v(-5.69, -2.93) * mm});
            skLineSegment(sketch, "E175.0.66", {"start": v(-5.69, -2.93) * mm, "end": v(-5.73, -3.08) * mm});
            skArc(sketch, "E175.0.67", {"start": v(-5.73, -3.08) * mm, "mid": v(-5.63, -3.25) * mm, "end": v(-5.53, -3.42) * mm});
            skLineSegment(sketch, "E175.0.68", {"start": v(-5.53, -3.42) * mm, "end": v(-5.38, -3.46) * mm});
            skArc(sketch, "E175.0.69", {"start": v(-5.38, -3.46) * mm, "mid": v(-5.18, -3.76) * mm, "end": v(-4.95, -4.05) * mm});
            skLineSegment(sketch, "E175.0.70", {"start": v(-4.95, -4.05) * mm, "end": v(-4.96, -4.2) * mm});
            skArc(sketch, "E175.0.71", {"start": v(-4.96, -4.2) * mm, "mid": v(-4.83, -4.35) * mm, "end": v(-4.7, -4.5) * mm});
            skLineSegment(sketch, "E175.0.72", {"start": v(-4.7, -4.5) * mm, "end": v(-4.55, -4.5) * mm});
            skArc(sketch, "E175.0.73", {"start": v(-4.55, -4.5) * mm, "mid": v(-4.28, -4.76) * mm, "end": v(-4, -5) * mm});
            skLineSegment(sketch, "E175.0.74", {"start": v(-4, -5) * mm, "end": v(-3.98, -5.14) * mm});
            skArc(sketch, "E175.0.75", {"start": v(-3.98, -5.14) * mm, "mid": v(-3.82, -5.26) * mm, "end": v(-3.66, -5.37) * mm});
            skLineSegment(sketch, "E175.0.76", {"start": v(-3.66, -5.37) * mm, "end": v(-3.51, -5.35) * mm});
            skArc(sketch, "E175.0.77", {"start": v(-3.51, -5.35) * mm, "mid": v(-3.2, -5.54) * mm, "end": v(-2.88, -5.72) * mm});
            skLineSegment(sketch, "E175.0.78", {"start": v(-2.88, -5.72) * mm, "end": v(-2.83, -5.85) * mm});
            skArc(sketch, "E175.0.79", {"start": v(-2.83, -5.85) * mm, "mid": v(-2.64, -5.94) * mm, "end": v(-2.46, -6.02) * mm});
            skLineSegment(sketch, "E175.0.80", {"start": v(-2.46, -6.02) * mm, "end": v(-2.32, -5.96) * mm});
            skArc(sketch, "E175.0.81", {"start": v(-2.32, -5.96) * mm, "mid": v(-1.98, -6.09) * mm, "end": v(-1.63, -6.19) * mm});
            skLineSegment(sketch, "E175.0.82", {"start": v(-1.63, -6.19) * mm, "end": v(-1.55, -6.31) * mm});
            skArc(sketch, "E175.0.83", {"start": v(-1.55, -6.31) * mm, "mid": v(-1.35, -6.36) * mm, "end": v(-1.16, -6.4) * mm});
            skLineSegment(sketch, "E175.0.84", {"start": v(-1.16, -6.4) * mm, "end": v(-1.03, -6.32) * mm});
            skArc(sketch, "E175.0.85", {"start": v(-1.03, -6.32) * mm, "mid": v(-0.67, -6.36) * mm, "end": v(-0.3, -6.4) * mm});
            skLineSegment(sketch, "E175.0.86", {"start": v(-0.3, -6.4) * mm, "end": v(-0.2, -6.5) * mm});
            skArc(sketch, "E175.0.87", {"start": v(-0.2, -6.5) * mm, "mid": v(0, -6.5) * mm, "end": v(0.2, -6.5) * mm});
            skLineSegment(sketch, "E175.0.88", {"start": v(0.2, -6.5) * mm, "end": v(0.3, -6.4) * mm});
            skArc(sketch, "E175.0.89", {"start": v(0.3, -6.4) * mm, "mid": v(0.67, -6.36) * mm, "end": v(1.03, -6.32) * mm});
            skLineSegment(sketch, "E175.0.90", {"start": v(1.03, -6.32) * mm, "end": v(1.16, -6.4) * mm});
            skArc(sketch, "E175.0.91", {"start": v(1.16, -6.4) * mm, "mid": v(1.35, -6.36) * mm, "end": v(1.55, -6.31) * mm});
            skLineSegment(sketch, "E175.0.92", {"start": v(1.55, -6.31) * mm, "end": v(1.63, -6.19) * mm});
            skArc(sketch, "E175.0.93", {"start": v(1.63, -6.19) * mm, "mid": v(1.98, -6.09) * mm, "end": v(2.32, -5.96) * mm});
            skLineSegment(sketch, "E175.0.94", {"start": v(2.32, -5.96) * mm, "end": v(2.46, -6.02) * mm});
            skArc(sketch, "E175.0.95", {"start": v(2.46, -6.02) * mm, "mid": v(2.64, -5.94) * mm, "end": v(2.83, -5.85) * mm});
            skLineSegment(sketch, "E175.0.96", {"start": v(2.83, -5.85) * mm, "end": v(2.88, -5.72) * mm});
            skArc(sketch, "E175.0.97", {"start": v(2.88, -5.72) * mm, "mid": v(3.2, -5.54) * mm, "end": v(3.51, -5.35) * mm});
            skLineSegment(sketch, "E175.0.98", {"start": v(3.51, -5.35) * mm, "end": v(3.66, -5.37) * mm});
            skArc(sketch, "E175.0.99", {"start": v(3.66, -5.37) * mm, "mid": v(3.82, -5.26) * mm, "end": v(3.98, -5.14) * mm});
            skLineSegment(sketch, "E175.0.100", {"start": v(3.98, -5.14) * mm, "end": v(4, -5) * mm});
            skArc(sketch, "E175.0.101", {"start": v(4, -5) * mm, "mid": v(4.28, -4.76) * mm, "end": v(4.55, -4.5) * mm});
            skLineSegment(sketch, "E175.0.102", {"start": v(4.55, -4.5) * mm, "end": v(4.7, -4.5) * mm});
            skArc(sketch, "E175.0.103", {"start": v(4.7, -4.5) * mm, "mid": v(4.83, -4.35) * mm, "end": v(4.96, -4.2) * mm});
            skLineSegment(sketch, "E175.0.104", {"start": v(4.96, -4.2) * mm, "end": v(4.95, -4.05) * mm});
            skArc(sketch, "E175.0.105", {"start": v(4.95, -4.05) * mm, "mid": v(5.18, -3.76) * mm, "end": v(5.38, -3.46) * mm});
            skLineSegment(sketch, "E175.0.106", {"start": v(5.38, -3.46) * mm, "end": v(5.53, -3.42) * mm});
            skArc(sketch, "E175.0.107", {"start": v(5.53, -3.42) * mm, "mid": v(5.63, -3.25) * mm, "end": v(5.73, -3.08) * mm});
            skLineSegment(sketch, "E175.0.108", {"start": v(5.73, -3.08) * mm, "end": v(5.69, -2.93) * mm});
            skArc(sketch, "E175.0.109", {"start": v(5.69, -2.93) * mm, "mid": v(5.85, -2.6) * mm, "end": v(5.99, -2.26) * mm});
            skLineSegment(sketch, "E175.0.110", {"start": v(5.99, -2.26) * mm, "end": v(6.12, -2.2) * mm});
            skArc(sketch, "E175.0.111", {"start": v(6.12, -2.2) * mm, "mid": v(6.18, -2) * mm, "end": v(6.24, -1.82) * mm});
            skLineSegment(sketch, "E175.0.112", {"start": v(6.24, -1.82) * mm, "end": v(6.17, -1.69) * mm});
            skArc(sketch, "E175.0.113", {"start": v(6.17, -1.69) * mm, "mid": v(6.26, -1.33) * mm, "end": v(6.33, -0.97) * mm});
            skLineSegment(sketch, "E175.0.114", {"start": v(6.33, -0.97) * mm, "end": v(6.44, -0.88) * mm});
            skArc(sketch, "E175.0.115", {"start": v(6.44, -0.88) * mm, "mid": v(6.46, -0.68) * mm, "end": v(6.48, -0.48) * mm});
            skLineSegment(sketch, "E175.0.116", {"start": v(6.48, -0.48) * mm, "end": v(6.39, -0.37) * mm});
            skArc(sketch, "E175.0.117", {"start": v(6.39, -0.37) * mm, "mid": v(6.4, 0) * mm, "end": v(6.39, 0.37) * mm});
            skLineSegment(sketch, "E175.0.118", {"start": v(6.39, 0.37) * mm, "end": v(6.48, 0.48) * mm});
            skArc(sketch, "E175.0.119", {"start": v(6.48, 0.48) * mm, "mid": v(6.46, 0.68) * mm, "end": v(6.44, 0.88) * mm});
            skSolve(sketch);
        }
        {
            var Q0;
            Q0=makeQuery(id+"F5.imprint","IMPRINT",FACE,{"disambiguationData":[TD([[makeQuery(id+"F5.imprint","IMPRINT",EDGE,{"derivedFrom":sQuery(id+"F5.wireOp",EDGE,"E174")}),-1.0]])]});
            extrude(context, id + "F6", {"entities" : qUnion([Q0]), "operationType" : NewBodyOperationType.ADD, "depth" : (getVariable(context, 'Bore_Depth_F')) * mm});
        }
        {
            var Q0;
            Q0=makeQuery(id+"F4.opExtrude","CAP_FACE",FACE,{"disambiguationData":[OSD([sQuery(id+"F3.wireOp",EDGE,"E0"),sQuery(id+"F3.wireOp",EDGE,"E1"),sQuery(id+"F3.wireOp",EDGE,"E2"),sQuery(id+"F3.wireOp",EDGE,"E3"),sQuery(id+"F3.wireOp",EDGE,"E4"),sQuery(id+"F3.wireOp",EDGE,"E5"),sQuery(id+"F3.wireOp",EDGE,"E6"),sQuery(id+"F3.wireOp",EDGE,"E7"),sQuery(id+"F3.wireOp",EDGE,"E8"),sQuery(id+"F3.wireOp",EDGE,"E9"),sQuery(id+"F3.wireOp",EDGE,"E10"),sQuery(id+"F3.wireOp",EDGE,"E11"),sQuery(id+"F3.wireOp",EDGE,"E12"),sQuery(id+"F3.wireOp",EDGE,"E13"),sQuery(id+"F3.wireOp",EDGE,"E14"),sQuery(id+"F3.wireOp",EDGE,"E15"),sQuery(id+"F3.wireOp",EDGE,"E16"),sQuery(id+"F3.wireOp",EDGE,"E17"),sQuery(id+"F3.wireOp",EDGE,"E18"),sQuery(id+"F3.wireOp",EDGE,"E19"),sQuery(id+"F3.wireOp",EDGE,"E20"),sQuery(id+"F3.wireOp",EDGE,"E21"),sQuery(id+"F3.wireOp",EDGE,"E22"),sQuery(id+"F3.wireOp",EDGE,"E23"),sQuery(id+"F3.wireOp",EDGE,"E24"),sQuery(id+"F3.wireOp",EDGE,"E25"),sQuery(id+"F3.wireOp",EDGE,"E26"),sQuery(id+"F3.wireOp",EDGE,"E27"),sQuery(id+"F3.wireOp",EDGE,"E28"),sQuery(id+"F3.wireOp",EDGE,"E29"),sQuery(id+"F3.wireOp",EDGE,"E30"),sQuery(id+"F3.wireOp",EDGE,"E31"),sQuery(id+"F3.wireOp",EDGE,"E32"),sQuery(id+"F3.wireOp",EDGE,"E33"),sQuery(id+"F3.wireOp",EDGE,"E34"),sQuery(id+"F3.wireOp",EDGE,"E35"),sQuery(id+"F3.wireOp",EDGE,"E36"),sQuery(id+"F3.wireOp",EDGE,"E37"),sQuery(id+"F3.wireOp",EDGE,"E38"),sQuery(id+"F3.wireOp",EDGE,"E39"),sQuery(id+"F3.wireOp",EDGE,"E40"),sQuery(id+"F3.wireOp",EDGE,"E41"),sQuery(id+"F3.wireOp",EDGE,"E42"),sQuery(id+"F3.wireOp",EDGE,"E43"),sQuery(id+"F3.wireOp",EDGE,"E44"),sQuery(id+"F3.wireOp",EDGE,"E45"),sQuery(id+"F3.wireOp",EDGE,"E46"),sQuery(id+"F3.wireOp",EDGE,"E47"),sQuery(id+"F3.wireOp",EDGE,"E48"),sQuery(id+"F3.wireOp",EDGE,"E49"),sQuery(id+"F3.wireOp",EDGE,"E50"),sQuery(id+"F3.wireOp",EDGE,"E51"),sQuery(id+"F3.wireOp",EDGE,"E52"),sQuery(id+"F3.wireOp",EDGE,"E53"),sQuery(id+"F3.wireOp",EDGE,"E54"),sQuery(id+"F3.wireOp",EDGE,"E55"),sQuery(id+"F3.wireOp",EDGE,"E56"),sQuery(id+"F3.wireOp",EDGE,"E57"),sQuery(id+"F3.wireOp",EDGE,"E58"),sQuery(id+"F3.wireOp",EDGE,"E59"),sQuery(id+"F3.wireOp",EDGE,"E60"),sQuery(id+"F3.wireOp",EDGE,"E61"),sQuery(id+"F3.wireOp",EDGE,"E62"),sQuery(id+"F3.wireOp",EDGE,"E63"),sQuery(id+"F3.wireOp",EDGE,"E64"),sQuery(id+"F3.wireOp",EDGE,"E65"),sQuery(id+"F3.wireOp",EDGE,"E66"),sQuery(id+"F3.wireOp",EDGE,"E67"),sQuery(id+"F3.wireOp",EDGE,"E68"),sQuery(id+"F3.wireOp",EDGE,"E69"),sQuery(id+"F3.wireOp",EDGE,"E70"),sQuery(id+"F3.wireOp",EDGE,"E71"),sQuery(id+"F3.wireOp",EDGE,"E72"),sQuery(id+"F3.wireOp",EDGE,"E73"),sQuery(id+"F3.wireOp",EDGE,"E74"),sQuery(id+"F3.wireOp",EDGE,"E75"),sQuery(id+"F3.wireOp",EDGE,"E76"),sQuery(id+"F3.wireOp",EDGE,"E77"),sQuery(id+"F3.wireOp",EDGE,"E78"),sQuery(id+"F3.wireOp",EDGE,"E79"),sQuery(id+"F3.wireOp",EDGE,"E80"),sQuery(id+"F3.wireOp",EDGE,"E81"),sQuery(id+"F3.wireOp",EDGE,"E82"),sQuery(id+"F3.wireOp",EDGE,"E83"),sQuery(id+"F3.wireOp",EDGE,"E84"),sQuery(id+"F3.wireOp",EDGE,"E85"),sQuery(id+"F3.wireOp",EDGE,"E86"),sQuery(id+"F3.wireOp",EDGE,"E87"),sQuery(id+"F3.wireOp",EDGE,"E88"),sQuery(id+"F3.wireOp",EDGE,"E89"),sQuery(id+"F3.wireOp",EDGE,"E90"),sQuery(id+"F3.wireOp",EDGE,"E91"),sQuery(id+"F3.wireOp",EDGE,"E92"),sQuery(id+"F3.wireOp",EDGE,"E93"),sQuery(id+"F3.wireOp",EDGE,"E94"),sQuery(id+"F3.wireOp",EDGE,"E95"),sQuery(id+"F3.wireOp",EDGE,"E96"),sQuery(id+"F3.wireOp",EDGE,"E97"),sQuery(id+"F3.wireOp",EDGE,"E98"),sQuery(id+"F3.wireOp",EDGE,"E99"),sQuery(id+"F3.wireOp",EDGE,"E100"),sQuery(id+"F3.wireOp",EDGE,"E101"),sQuery(id+"F3.wireOp",EDGE,"E102"),sQuery(id+"F3.wireOp",EDGE,"E103"),sQuery(id+"F3.wireOp",EDGE,"E104"),sQuery(id+"F3.wireOp",EDGE,"E105"),sQuery(id+"F3.wireOp",EDGE,"E106"),sQuery(id+"F3.wireOp",EDGE,"E107"),sQuery(id+"F3.wireOp",EDGE,"E108"),sQuery(id+"F3.wireOp",EDGE,"E109"),sQuery(id+"F3.wireOp",EDGE,"E110"),sQuery(id+"F3.wireOp",EDGE,"E111"),sQuery(id+"F3.wireOp",EDGE,"E112"),sQuery(id+"F3.wireOp",EDGE,"E113"),sQuery(id+"F3.wireOp",EDGE,"E114"),sQuery(id+"F3.wireOp",EDGE,"E115"),sQuery(id+"F3.wireOp",EDGE,"E116"),sQuery(id+"F3.wireOp",EDGE,"E117"),sQuery(id+"F3.wireOp",EDGE,"E118"),sQuery(id+"F3.wireOp",EDGE,"E119"),sQuery(id+"F3.wireOp",EDGE,"E120"),sQuery(id+"F3.wireOp",EDGE,"E121"),sQuery(id+"F3.wireOp",EDGE,"E122"),sQuery(id+"F3.wireOp",EDGE,"E123"),sQuery(id+"F3.wireOp",EDGE,"E124"),sQuery(id+"F3.wireOp",EDGE,"E125"),sQuery(id+"F3.wireOp",EDGE,"E126"),sQuery(id+"F3.wireOp",EDGE,"E127"),sQuery(id+"F3.wireOp",EDGE,"E128"),sQuery(id+"F3.wireOp",EDGE,"E129"),sQuery(id+"F3.wireOp",EDGE,"E130"),sQuery(id+"F3.wireOp",EDGE,"E131"),sQuery(id+"F3.wireOp",EDGE,"E132"),sQuery(id+"F3.wireOp",EDGE,"E133"),sQuery(id+"F3.wireOp",EDGE,"E134"),sQuery(id+"F3.wireOp",EDGE,"E135"),sQuery(id+"F3.wireOp",EDGE,"E136"),sQuery(id+"F3.wireOp",EDGE,"E137"),sQuery(id+"F3.wireOp",EDGE,"E138"),sQuery(id+"F3.wireOp",EDGE,"E139"),sQuery(id+"F3.wireOp",EDGE,"E140"),sQuery(id+"F3.wireOp",EDGE,"E141"),sQuery(id+"F3.wireOp",EDGE,"E142"),sQuery(id+"F3.wireOp",EDGE,"E143"),sQuery(id+"F3.wireOp",EDGE,"E144"),sQuery(id+"F3.wireOp",EDGE,"E145"),sQuery(id+"F3.wireOp",EDGE,"E146"),sQuery(id+"F3.wireOp",EDGE,"E147"),sQuery(id+"F3.wireOp",EDGE,"E148"),sQuery(id+"F3.wireOp",EDGE,"E149"),sQuery(id+"F3.wireOp",EDGE,"E150"),sQuery(id+"F3.wireOp",EDGE,"E151"),sQuery(id+"F3.wireOp",EDGE,"E152"),sQuery(id+"F3.wireOp",EDGE,"E153"),sQuery(id+"F3.wireOp",EDGE,"E154"),sQuery(id+"F3.wireOp",EDGE,"E155"),sQuery(id+"F3.wireOp",EDGE,"E156"),sQuery(id+"F3.wireOp",EDGE,"E157"),sQuery(id+"F3.wireOp",EDGE,"E158"),sQuery(id+"F3.wireOp",EDGE,"E159"),sQuery(id+"F3.wireOp",EDGE,"E160"),sQuery(id+"F3.wireOp",EDGE,"E161"),sQuery(id+"F3.wireOp",EDGE,"E162"),sQuery(id+"F3.wireOp",EDGE,"E163"),sQuery(id+"F3.wireOp",EDGE,"E164"),sQuery(id+"F3.wireOp",EDGE,"E165"),sQuery(id+"F3.wireOp",EDGE,"E166"),sQuery(id+"F3.wireOp",EDGE,"E167"),sQuery(id+"F3.wireOp",EDGE,"E168"),sQuery(id+"F3.wireOp",EDGE,"E169"),sQuery(id+"F3.wireOp",EDGE,"E170"),sQuery(id+"F3.wireOp",EDGE,"E171"),sQuery(id+"F3.wireOp",EDGE,"E172"),sQuery(id+"F3.wireOp",EDGE,"E173")])],"isStart":true});
            var sketch = newSketch(context, id + "F7", { "sketchPlane" : qUnion([Q0])});
            skCircle(sketch, "E176", {"center": v(0, 0) * mm, "radius": 5.75 * mm});
            skLineSegment(sketch, "E177.0.0", {"start": v(-6.33, 0.97) * mm, "end": v(-6.44, 0.88) * mm});
            skArc(sketch, "E177.0.1", {"start": v(-6.44, 0.88) * mm, "mid": v(-6.46, 0.68) * mm, "end": v(-6.48, 0.48) * mm});
            skLineSegment(sketch, "E177.0.2", {"start": v(-6.48, 0.48) * mm, "end": v(-6.39, 0.37) * mm});
            skArc(sketch, "E177.0.3", {"start": v(-6.39, 0.37) * mm, "mid": v(-6.4, 0) * mm, "end": v(-6.39, -0.37) * mm});
            skLineSegment(sketch, "E177.0.4", {"start": v(-6.39, -0.37) * mm, "end": v(-6.48, -0.48) * mm});
            skArc(sketch, "E177.0.5", {"start": v(-6.48, -0.48) * mm, "mid": v(-6.46, -0.68) * mm, "end": v(-6.44, -0.88) * mm});
            skLineSegment(sketch, "E177.0.6", {"start": v(-6.44, -0.88) * mm, "end": v(-6.33, -0.97) * mm});
            skArc(sketch, "E177.0.7", {"start": v(-6.33, -0.97) * mm, "mid": v(-6.26, -1.33) * mm, "end": v(-6.17, -1.69) * mm});
            skLineSegment(sketch, "E177.0.8", {"start": v(-6.17, -1.69) * mm, "end": v(-6.24, -1.82) * mm});
            skArc(sketch, "E177.0.9", {"start": v(-6.24, -1.82) * mm, "mid": v(-6.18, -2) * mm, "end": v(-6.12, -2.2) * mm});
            skLineSegment(sketch, "E177.0.10", {"start": v(-6.12, -2.2) * mm, "end": v(-5.99, -2.26) * mm});
            skArc(sketch, "E177.0.11", {"start": v(-5.99, -2.26) * mm, "mid": v(-5.85, -2.6) * mm, "end": v(-5.69, -2.93) * mm});
            skLineSegment(sketch, "E177.0.12", {"start": v(-5.69, -2.93) * mm, "end": v(-5.73, -3.08) * mm});
            skArc(sketch, "E177.0.13", {"start": v(-5.73, -3.08) * mm, "mid": v(-5.63, -3.25) * mm, "end": v(-5.53, -3.42) * mm});
            skLineSegment(sketch, "E177.0.14", {"start": v(-5.53, -3.42) * mm, "end": v(-5.38, -3.46) * mm});
            skArc(sketch, "E177.0.15", {"start": v(-5.38, -3.46) * mm, "mid": v(-5.18, -3.76) * mm, "end": v(-4.95, -4.05) * mm});
            skLineSegment(sketch, "E177.0.16", {"start": v(-4.95, -4.05) * mm, "end": v(-4.96, -4.2) * mm});
            skArc(sketch, "E177.0.17", {"start": v(-4.96, -4.2) * mm, "mid": v(-4.83, -4.35) * mm, "end": v(-4.7, -4.5) * mm});
            skLineSegment(sketch, "E177.0.18", {"start": v(-4.7, -4.5) * mm, "end": v(-4.55, -4.5) * mm});
            skArc(sketch, "E177.0.19", {"start": v(-4.55, -4.5) * mm, "mid": v(-4.28, -4.76) * mm, "end": v(-4, -5) * mm});
            skLineSegment(sketch, "E177.0.20", {"start": v(-4, -5) * mm, "end": v(-3.98, -5.14) * mm});
            skArc(sketch, "E177.0.21", {"start": v(-3.98, -5.14) * mm, "mid": v(-3.82, -5.26) * mm, "end": v(-3.66, -5.37) * mm});
            skLineSegment(sketch, "E177.0.22", {"start": v(-3.66, -5.37) * mm, "end": v(-3.51, -5.35) * mm});
            skArc(sketch, "E177.0.23", {"start": v(-3.51, -5.35) * mm, "mid": v(-3.2, -5.54) * mm, "end": v(-2.88, -5.72) * mm});
            skLineSegment(sketch, "E177.0.24", {"start": v(-2.88, -5.72) * mm, "end": v(-2.83, -5.85) * mm});
            skArc(sketch, "E177.0.25", {"start": v(-2.83, -5.85) * mm, "mid": v(-2.64, -5.94) * mm, "end": v(-2.46, -6.02) * mm});
            skLineSegment(sketch, "E177.0.26", {"start": v(-2.46, -6.02) * mm, "end": v(-2.32, -5.96) * mm});
            skArc(sketch, "E177.0.27", {"start": v(-2.32, -5.96) * mm, "mid": v(-1.98, -6.09) * mm, "end": v(-1.63, -6.19) * mm});
            skLineSegment(sketch, "E177.0.28", {"start": v(-1.63, -6.19) * mm, "end": v(-1.55, -6.31) * mm});
            skArc(sketch, "E177.0.29", {"start": v(-1.55, -6.31) * mm, "mid": v(-1.35, -6.36) * mm, "end": v(-1.16, -6.4) * mm});
            skLineSegment(sketch, "E177.0.30", {"start": v(-1.16, -6.4) * mm, "end": v(-1.03, -6.32) * mm});
            skArc(sketch, "E177.0.31", {"start": v(-1.03, -6.32) * mm, "mid": v(-0.67, -6.36) * mm, "end": v(-0.3, -6.4) * mm});
            skLineSegment(sketch, "E177.0.32", {"start": v(-0.3, -6.4) * mm, "end": v(-0.2, -6.5) * mm});
            skArc(sketch, "E177.0.33", {"start": v(-0.2, -6.5) * mm, "mid": v(0, -6.5) * mm, "end": v(0.2, -6.5) * mm});
            skLineSegment(sketch, "E177.0.34", {"start": v(0.2, -6.5) * mm, "end": v(0.3, -6.4) * mm});
            skArc(sketch, "E177.0.35", {"start": v(0.3, -6.4) * mm, "mid": v(0.67, -6.36) * mm, "end": v(1.03, -6.32) * mm});
            skLineSegment(sketch, "E177.0.36", {"start": v(1.03, -6.32) * mm, "end": v(1.16, -6.4) * mm});
            skArc(sketch, "E177.0.37", {"start": v(1.16, -6.4) * mm, "mid": v(1.35, -6.36) * mm, "end": v(1.55, -6.31) * mm});
            skLineSegment(sketch, "E177.0.38", {"start": v(1.55, -6.31) * mm, "end": v(1.63, -6.19) * mm});
            skArc(sketch, "E177.0.39", {"start": v(1.63, -6.19) * mm, "mid": v(1.98, -6.09) * mm, "end": v(2.32, -5.96) * mm});
            skLineSegment(sketch, "E177.0.40", {"start": v(2.32, -5.96) * mm, "end": v(2.46, -6.02) * mm});
            skArc(sketch, "E177.0.41", {"start": v(2.46, -6.02) * mm, "mid": v(2.64, -5.94) * mm, "end": v(2.83, -5.85) * mm});
            skLineSegment(sketch, "E177.0.42", {"start": v(2.83, -5.85) * mm, "end": v(2.88, -5.72) * mm});
            skArc(sketch, "E177.0.43", {"start": v(2.88, -5.72) * mm, "mid": v(3.2, -5.54) * mm, "end": v(3.51, -5.35) * mm});
            skLineSegment(sketch, "E177.0.44", {"start": v(3.51, -5.35) * mm, "end": v(3.66, -5.37) * mm});
            skArc(sketch, "E177.0.45", {"start": v(3.66, -5.37) * mm, "mid": v(3.82, -5.26) * mm, "end": v(3.98, -5.14) * mm});
            skLineSegment(sketch, "E177.0.46", {"start": v(3.98, -5.14) * mm, "end": v(4, -5) * mm});
            skArc(sketch, "E177.0.47", {"start": v(4, -5) * mm, "mid": v(4.28, -4.76) * mm, "end": v(4.55, -4.5) * mm});
            skLineSegment(sketch, "E177.0.48", {"start": v(4.55, -4.5) * mm, "end": v(4.7, -4.5) * mm});
            skArc(sketch, "E177.0.49", {"start": v(4.7, -4.5) * mm, "mid": v(4.83, -4.35) * mm, "end": v(4.96, -4.2) * mm});
            skLineSegment(sketch, "E177.0.50", {"start": v(4.96, -4.2) * mm, "end": v(4.95, -4.05) * mm});
            skArc(sketch, "E177.0.51", {"start": v(4.95, -4.05) * mm, "mid": v(5.18, -3.76) * mm, "end": v(5.38, -3.46) * mm});
            skLineSegment(sketch, "E177.0.52", {"start": v(5.38, -3.46) * mm, "end": v(5.53, -3.42) * mm});
            skArc(sketch, "E177.0.53", {"start": v(5.53, -3.42) * mm, "mid": v(5.63, -3.25) * mm, "end": v(5.73, -3.08) * mm});
            skLineSegment(sketch, "E177.0.54", {"start": v(5.73, -3.08) * mm, "end": v(5.69, -2.93) * mm});
            skArc(sketch, "E177.0.55", {"start": v(5.69, -2.93) * mm, "mid": v(5.85, -2.6) * mm, "end": v(5.99, -2.26) * mm});
            skLineSegment(sketch, "E177.0.56", {"start": v(5.99, -2.26) * mm, "end": v(6.12, -2.2) * mm});
            skArc(sketch, "E177.0.57", {"start": v(6.12, -2.2) * mm, "mid": v(6.18, -2) * mm, "end": v(6.24, -1.82) * mm});
            skLineSegment(sketch, "E177.0.58", {"start": v(6.24, -1.82) * mm, "end": v(6.17, -1.69) * mm});
            skArc(sketch, "E177.0.59", {"start": v(6.17, -1.69) * mm, "mid": v(6.26, -1.33) * mm, "end": v(6.33, -0.97) * mm});
            skLineSegment(sketch, "E177.0.60", {"start": v(6.33, -0.97) * mm, "end": v(6.44, -0.88) * mm});
            skArc(sketch, "E177.0.61", {"start": v(6.44, -0.88) * mm, "mid": v(6.46, -0.68) * mm, "end": v(6.48, -0.48) * mm});
            skLineSegment(sketch, "E177.0.62", {"start": v(6.48, -0.48) * mm, "end": v(6.39, -0.37) * mm});
            skArc(sketch, "E177.0.63", {"start": v(6.39, -0.37) * mm, "mid": v(6.4, 0) * mm, "end": v(6.39, 0.37) * mm});
            skLineSegment(sketch, "E177.0.64", {"start": v(6.39, 0.37) * mm, "end": v(6.48, 0.48) * mm});
            skArc(sketch, "E177.0.65", {"start": v(6.48, 0.48) * mm, "mid": v(6.46, 0.68) * mm, "end": v(6.44, 0.88) * mm});
            skLineSegment(sketch, "E177.0.66", {"start": v(6.44, 0.88) * mm, "end": v(6.33, 0.97) * mm});
            skArc(sketch, "E177.0.67", {"start": v(6.33, 0.97) * mm, "mid": v(6.26, 1.33) * mm, "end": v(6.17, 1.69) * mm});
            skLineSegment(sketch, "E177.0.68", {"start": v(6.17, 1.69) * mm, "end": v(6.24, 1.82) * mm});
            skArc(sketch, "E177.0.69", {"start": v(6.24, 1.82) * mm, "mid": v(6.18, 2) * mm, "end": v(6.12, 2.2) * mm});
            skLineSegment(sketch, "E177.0.70", {"start": v(6.12, 2.2) * mm, "end": v(5.99, 2.26) * mm});
            skArc(sketch, "E177.0.71", {"start": v(5.99, 2.26) * mm, "mid": v(5.85, 2.6) * mm, "end": v(5.69, 2.93) * mm});
            skLineSegment(sketch, "E177.0.72", {"start": v(5.69, 2.93) * mm, "end": v(5.73, 3.08) * mm});
            skArc(sketch, "E177.0.73", {"start": v(5.73, 3.08) * mm, "mid": v(5.63, 3.25) * mm, "end": v(5.53, 3.42) * mm});
            skLineSegment(sketch, "E177.0.74", {"start": v(5.53, 3.42) * mm, "end": v(5.38, 3.46) * mm});
            skArc(sketch, "E177.0.75", {"start": v(5.38, 3.46) * mm, "mid": v(5.18, 3.76) * mm, "end": v(4.95, 4.05) * mm});
            skLineSegment(sketch, "E177.0.76", {"start": v(4.95, 4.05) * mm, "end": v(4.96, 4.2) * mm});
            skArc(sketch, "E177.0.77", {"start": v(4.96, 4.2) * mm, "mid": v(4.83, 4.35) * mm, "end": v(4.7, 4.5) * mm});
            skLineSegment(sketch, "E177.0.78", {"start": v(4.7, 4.5) * mm, "end": v(4.55, 4.5) * mm});
            skArc(sketch, "E177.0.79", {"start": v(4.55, 4.5) * mm, "mid": v(4.28, 4.76) * mm, "end": v(4, 5) * mm});
            skLineSegment(sketch, "E177.0.80", {"start": v(4, 5) * mm, "end": v(3.98, 5.14) * mm});
            skArc(sketch, "E177.0.81", {"start": v(3.98, 5.14) * mm, "mid": v(3.82, 5.26) * mm, "end": v(3.66, 5.37) * mm});
            skLineSegment(sketch, "E177.0.82", {"start": v(3.66, 5.37) * mm, "end": v(3.51, 5.35) * mm});
            skArc(sketch, "E177.0.83", {"start": v(3.51, 5.35) * mm, "mid": v(3.2, 5.54) * mm, "end": v(2.88, 5.72) * mm});
            skLineSegment(sketch, "E177.0.84", {"start": v(2.88, 5.72) * mm, "end": v(2.83, 5.85) * mm});
            skArc(sketch, "E177.0.85", {"start": v(2.83, 5.85) * mm, "mid": v(2.64, 5.94) * mm, "end": v(2.46, 6.02) * mm});
            skLineSegment(sketch, "E177.0.86", {"start": v(2.46, 6.02) * mm, "end": v(2.32, 5.96) * mm});
            skArc(sketch, "E177.0.87", {"start": v(2.32, 5.96) * mm, "mid": v(1.98, 6.09) * mm, "end": v(1.63, 6.19) * mm});
            skLineSegment(sketch, "E177.0.88", {"start": v(1.63, 6.19) * mm, "end": v(1.55, 6.31) * mm});
            skArc(sketch, "E177.0.89", {"start": v(1.55, 6.31) * mm, "mid": v(1.35, 6.36) * mm, "end": v(1.16, 6.4) * mm});
            skLineSegment(sketch, "E177.0.90", {"start": v(1.16, 6.4) * mm, "end": v(1.03, 6.32) * mm});
            skArc(sketch, "E177.0.91", {"start": v(1.03, 6.32) * mm, "mid": v(0.67, 6.36) * mm, "end": v(0.3, 6.4) * mm});
            skLineSegment(sketch, "E177.0.92", {"start": v(0.3, 6.4) * mm, "end": v(0.2, 6.5) * mm});
            skArc(sketch, "E177.0.93", {"start": v(0.2, 6.5) * mm, "mid": v(0, 6.5) * mm, "end": v(-0.2, 6.5) * mm});
            skLineSegment(sketch, "E177.0.94", {"start": v(-0.2, 6.5) * mm, "end": v(-0.3, 6.4) * mm});
            skArc(sketch, "E177.0.95", {"start": v(-0.3, 6.4) * mm, "mid": v(-0.67, 6.36) * mm, "end": v(-1.03, 6.32) * mm});
            skLineSegment(sketch, "E177.0.96", {"start": v(-1.03, 6.32) * mm, "end": v(-1.16, 6.4) * mm});
            skArc(sketch, "E177.0.97", {"start": v(-1.16, 6.4) * mm, "mid": v(-1.35, 6.36) * mm, "end": v(-1.55, 6.31) * mm});
            skLineSegment(sketch, "E177.0.98", {"start": v(-1.55, 6.31) * mm, "end": v(-1.63, 6.19) * mm});
            skArc(sketch, "E177.0.99", {"start": v(-1.63, 6.19) * mm, "mid": v(-1.98, 6.09) * mm, "end": v(-2.32, 5.96) * mm});
            skLineSegment(sketch, "E177.0.100", {"start": v(-2.32, 5.96) * mm, "end": v(-2.46, 6.02) * mm});
            skArc(sketch, "E177.0.101", {"start": v(-2.46, 6.02) * mm, "mid": v(-2.64, 5.94) * mm, "end": v(-2.83, 5.85) * mm});
            skLineSegment(sketch, "E177.0.102", {"start": v(-2.83, 5.85) * mm, "end": v(-2.88, 5.72) * mm});
            skArc(sketch, "E177.0.103", {"start": v(-2.88, 5.72) * mm, "mid": v(-3.2, 5.54) * mm, "end": v(-3.51, 5.35) * mm});
            skLineSegment(sketch, "E177.0.104", {"start": v(-3.51, 5.35) * mm, "end": v(-3.66, 5.37) * mm});
            skArc(sketch, "E177.0.105", {"start": v(-3.66, 5.37) * mm, "mid": v(-3.82, 5.26) * mm, "end": v(-3.98, 5.14) * mm});
            skLineSegment(sketch, "E177.0.106", {"start": v(-3.98, 5.14) * mm, "end": v(-4, 5) * mm});
            skArc(sketch, "E177.0.107", {"start": v(-4, 5) * mm, "mid": v(-4.28, 4.76) * mm, "end": v(-4.55, 4.5) * mm});
            skLineSegment(sketch, "E177.0.108", {"start": v(-4.55, 4.5) * mm, "end": v(-4.7, 4.5) * mm});
            skArc(sketch, "E177.0.109", {"start": v(-4.7, 4.5) * mm, "mid": v(-4.83, 4.35) * mm, "end": v(-4.96, 4.2) * mm});
            skLineSegment(sketch, "E177.0.110", {"start": v(-4.96, 4.2) * mm, "end": v(-4.95, 4.05) * mm});
            skArc(sketch, "E177.0.111", {"start": v(-4.95, 4.05) * mm, "mid": v(-5.18, 3.76) * mm, "end": v(-5.38, 3.46) * mm});
            skLineSegment(sketch, "E177.0.112", {"start": v(-5.38, 3.46) * mm, "end": v(-5.53, 3.42) * mm});
            skArc(sketch, "E177.0.113", {"start": v(-5.53, 3.42) * mm, "mid": v(-5.63, 3.25) * mm, "end": v(-5.73, 3.08) * mm});
            skLineSegment(sketch, "E177.0.114", {"start": v(-5.73, 3.08) * mm, "end": v(-5.69, 2.93) * mm});
            skArc(sketch, "E177.0.115", {"start": v(-5.69, 2.93) * mm, "mid": v(-5.85, 2.6) * mm, "end": v(-5.99, 2.26) * mm});
            skLineSegment(sketch, "E177.0.116", {"start": v(-5.99, 2.26) * mm, "end": v(-6.12, 2.2) * mm});
            skArc(sketch, "E177.0.117", {"start": v(-6.12, 2.2) * mm, "mid": v(-6.18, 2) * mm, "end": v(-6.24, 1.82) * mm});
            skLineSegment(sketch, "E177.0.118", {"start": v(-6.24, 1.82) * mm, "end": v(-6.17, 1.69) * mm});
            skArc(sketch, "E177.0.119", {"start": v(-6.17, 1.69) * mm, "mid": v(-6.26, 1.33) * mm, "end": v(-6.33, 0.97) * mm});
            skSolve(sketch);
        }
        {
            var Q0;
            Q0=makeQuery(id+"F7.imprint","IMPRINT",FACE,{"disambiguationData":[TD([[makeQuery(id+"F7.imprint","IMPRINT",EDGE,{"derivedFrom":sQuery(id+"F7.wireOp",EDGE,"E176")}),-1.0]])]});
            extrude(context, id + "F8", {"entities" : qUnion([Q0]), "operationType" : NewBodyOperationType.ADD, "depth" : (getVariable(context, 'Bore_Depth_R')) * mm});
        }
        {
            var Q0;
            Q0=makeQuery(id+"F6.opExtrude","CAP_FACE",FACE,{"disambiguationData":[OSD([sQuery(id+"F5.wireOp",EDGE,"E174"),sQuery(id+"F5.wireOp",EDGE,"E175.0.0"),sQuery(id+"F5.wireOp",EDGE,"E175.0.1"),sQuery(id+"F5.wireOp",EDGE,"E175.0.2"),sQuery(id+"F5.wireOp",EDGE,"E175.0.3"),sQuery(id+"F5.wireOp",EDGE,"E175.0.4"),sQuery(id+"F5.wireOp",EDGE,"E175.0.5"),sQuery(id+"F5.wireOp",EDGE,"E175.0.6"),sQuery(id+"F5.wireOp",EDGE,"E175.0.7"),sQuery(id+"F5.wireOp",EDGE,"E175.0.8"),sQuery(id+"F5.wireOp",EDGE,"E175.0.9"),sQuery(id+"F5.wireOp",EDGE,"E175.0.10"),sQuery(id+"F5.wireOp",EDGE,"E175.0.11"),sQuery(id+"F5.wireOp",EDGE,"E175.0.12"),sQuery(id+"F5.wireOp",EDGE,"E175.0.13"),sQuery(id+"F5.wireOp",EDGE,"E175.0.14"),sQuery(id+"F5.wireOp",EDGE,"E175.0.15"),sQuery(id+"F5.wireOp",EDGE,"E175.0.16"),sQuery(id+"F5.wireOp",EDGE,"E175.0.17"),sQuery(id+"F5.wireOp",EDGE,"E175.0.18"),sQuery(id+"F5.wireOp",EDGE,"E175.0.19"),sQuery(id+"F5.wireOp",EDGE,"E175.0.20"),sQuery(id+"F5.wireOp",EDGE,"E175.0.21"),sQuery(id+"F5.wireOp",EDGE,"E175.0.22"),sQuery(id+"F5.wireOp",EDGE,"E175.0.23"),sQuery(id+"F5.wireOp",EDGE,"E175.0.24"),sQuery(id+"F5.wireOp",EDGE,"E175.0.25"),sQuery(id+"F5.wireOp",EDGE,"E175.0.26"),sQuery(id+"F5.wireOp",EDGE,"E175.0.27"),sQuery(id+"F5.wireOp",EDGE,"E175.0.28"),sQuery(id+"F5.wireOp",EDGE,"E175.0.29"),sQuery(id+"F5.wireOp",EDGE,"E175.0.30"),sQuery(id+"F5.wireOp",EDGE,"E175.0.31"),sQuery(id+"F5.wireOp",EDGE,"E175.0.32"),sQuery(id+"F5.wireOp",EDGE,"E175.0.33"),sQuery(id+"F5.wireOp",EDGE,"E175.0.34"),sQuery(id+"F5.wireOp",EDGE,"E175.0.35"),sQuery(id+"F5.wireOp",EDGE,"E175.0.36"),sQuery(id+"F5.wireOp",EDGE,"E175.0.37"),sQuery(id+"F5.wireOp",EDGE,"E175.0.38"),sQuery(id+"F5.wireOp",EDGE,"E175.0.39"),sQuery(id+"F5.wireOp",EDGE,"E175.0.40"),sQuery(id+"F5.wireOp",EDGE,"E175.0.41"),sQuery(id+"F5.wireOp",EDGE,"E175.0.42"),sQuery(id+"F5.wireOp",EDGE,"E175.0.43"),sQuery(id+"F5.wireOp",EDGE,"E175.0.44"),sQuery(id+"F5.wireOp",EDGE,"E175.0.45"),sQuery(id+"F5.wireOp",EDGE,"E175.0.46"),sQuery(id+"F5.wireOp",EDGE,"E175.0.47"),sQuery(id+"F5.wireOp",EDGE,"E175.0.48"),sQuery(id+"F5.wireOp",EDGE,"E175.0.49"),sQuery(id+"F5.wireOp",EDGE,"E175.0.50"),sQuery(id+"F5.wireOp",EDGE,"E175.0.51"),sQuery(id+"F5.wireOp",EDGE,"E175.0.52"),sQuery(id+"F5.wireOp",EDGE,"E175.0.53"),sQuery(id+"F5.wireOp",EDGE,"E175.0.54"),sQuery(id+"F5.wireOp",EDGE,"E175.0.55"),sQuery(id+"F5.wireOp",EDGE,"E175.0.56"),sQuery(id+"F5.wireOp",EDGE,"E175.0.57"),sQuery(id+"F5.wireOp",EDGE,"E175.0.58"),sQuery(id+"F5.wireOp",EDGE,"E175.0.59"),sQuery(id+"F5.wireOp",EDGE,"E175.0.60"),sQuery(id+"F5.wireOp",EDGE,"E175.0.61"),sQuery(id+"F5.wireOp",EDGE,"E175.0.62"),sQuery(id+"F5.wireOp",EDGE,"E175.0.63"),sQuery(id+"F5.wireOp",EDGE,"E175.0.64"),sQuery(id+"F5.wireOp",EDGE,"E175.0.65"),sQuery(id+"F5.wireOp",EDGE,"E175.0.66"),sQuery(id+"F5.wireOp",EDGE,"E175.0.67"),sQuery(id+"F5.wireOp",EDGE,"E175.0.68"),sQuery(id+"F5.wireOp",EDGE,"E175.0.69"),sQuery(id+"F5.wireOp",EDGE,"E175.0.70"),sQuery(id+"F5.wireOp",EDGE,"E175.0.71"),sQuery(id+"F5.wireOp",EDGE,"E175.0.72"),sQuery(id+"F5.wireOp",EDGE,"E175.0.73"),sQuery(id+"F5.wireOp",EDGE,"E175.0.74"),sQuery(id+"F5.wireOp",EDGE,"E175.0.75"),sQuery(id+"F5.wireOp",EDGE,"E175.0.76"),sQuery(id+"F5.wireOp",EDGE,"E175.0.77"),sQuery(id+"F5.wireOp",EDGE,"E175.0.78"),sQuery(id+"F5.wireOp",EDGE,"E175.0.79"),sQuery(id+"F5.wireOp",EDGE,"E175.0.80"),sQuery(id+"F5.wireOp",EDGE,"E175.0.81"),sQuery(id+"F5.wireOp",EDGE,"E175.0.82"),sQuery(id+"F5.wireOp",EDGE,"E175.0.83"),sQuery(id+"F5.wireOp",EDGE,"E175.0.84"),sQuery(id+"F5.wireOp",EDGE,"E175.0.85"),sQuery(id+"F5.wireOp",EDGE,"E175.0.86"),sQuery(id+"F5.wireOp",EDGE,"E175.0.87"),sQuery(id+"F5.wireOp",EDGE,"E175.0.88"),sQuery(id+"F5.wireOp",EDGE,"E175.0.89"),sQuery(id+"F5.wireOp",EDGE,"E175.0.90"),sQuery(id+"F5.wireOp",EDGE,"E175.0.91"),sQuery(id+"F5.wireOp",EDGE,"E175.0.92"),sQuery(id+"F5.wireOp",EDGE,"E175.0.93"),sQuery(id+"F5.wireOp",EDGE,"E175.0.94"),sQuery(id+"F5.wireOp",EDGE,"E175.0.95"),sQuery(id+"F5.wireOp",EDGE,"E175.0.96"),sQuery(id+"F5.wireOp",EDGE,"E175.0.97"),sQuery(id+"F5.wireOp",EDGE,"E175.0.98"),sQuery(id+"F5.wireOp",EDGE,"E175.0.99"),sQuery(id+"F5.wireOp",EDGE,"E175.0.100"),sQuery(id+"F5.wireOp",EDGE,"E175.0.101"),sQuery(id+"F5.wireOp",EDGE,"E175.0.102"),sQuery(id+"F5.wireOp",EDGE,"E175.0.103"),sQuery(id+"F5.wireOp",EDGE,"E175.0.104"),sQuery(id+"F5.wireOp",EDGE,"E175.0.105"),sQuery(id+"F5.wireOp",EDGE,"E175.0.106"),sQuery(id+"F5.wireOp",EDGE,"E175.0.107"),sQuery(id+"F5.wireOp",EDGE,"E175.0.108"),sQuery(id+"F5.wireOp",EDGE,"E175.0.109"),sQuery(id+"F5.wireOp",EDGE,"E175.0.110"),sQuery(id+"F5.wireOp",EDGE,"E175.0.111"),sQuery(id+"F5.wireOp",EDGE,"E175.0.112"),sQuery(id+"F5.wireOp",EDGE,"E175.0.113"),sQuery(id+"F5.wireOp",EDGE,"E175.0.114"),sQuery(id+"F5.wireOp",EDGE,"E175.0.115"),sQuery(id+"F5.wireOp",EDGE,"E175.0.116"),sQuery(id+"F5.wireOp",EDGE,"E175.0.117"),sQuery(id+"F5.wireOp",EDGE,"E175.0.118"),sQuery(id+"F5.wireOp",EDGE,"E175.0.119")])],"isStart":false});
            var sketch = newSketch(context, id + "F9", { "sketchPlane" : qUnion([Q0])});
            skCircle(sketch, "E178", {"center": v(0, 0) * mm, "radius": 6.5 * mm});
            skCircle(sketch, "E179", {"center": v(0, 0) * mm, "radius": 5.75 * mm});
            skSolve(sketch);
        }
        {
            var Q0;
            Q0=qSketchRegion(id+"F9",true);
            extrude(context, id + "F10", {"entities" : qUnion([Q0]), "oppositeDirection" : true, "depth" : (getVariable(context, 'Main_Length')) * mm});
        }
        {
            var Q0;
            Q0=qCreatedBy(makeId("Right.planeOp"),FACE);
            var sketch = newSketch(context, id + "F11", { "sketchPlane" : qUnion([Q0])});
            skCircle(sketch, "E180", {"center": v(-58, 0) * mm, "radius": 3.25 * mm});
            skPoint(sketch, "E181", {"position": v(-56.13, 0) * mm});
            skCircle(sketch, "E182", {"center": v(26, 0) * mm, "radius": 1.25 * mm});
            skCircle(sketch, "E183", {"center": v(-67, 0) * mm, "radius": 1.25 * mm});
            skSolve(sketch);
        }
        {
            var Q0;
            Q0=makeQuery(id+"F11.imprint","IMPRINT",FACE,{"disambiguationData":[TD([[makeQuery(id+"F11.imprint","IMPRINT",EDGE,{"derivedFrom":sQuery(id+"F11.wireOp",EDGE,"E180")}),1.0]])]});
            var Q1;
            Q1=makeQuery(id+"F11.imprint","IMPRINT",FACE,{"disambiguationData":[TD([[makeQuery(id+"F11.imprint","IMPRINT",EDGE,{"derivedFrom":sQuery(id+"F11.wireOp",EDGE,"E183")}),1.0]])]});
            extrude(context, id + "F12", {"entities" : qUnion([Q0, Q1]), "operationType" : NewBodyOperationType.REMOVE, "endBound" : BoundingType.THROUGH_ALL, "oppositeDirection" : true, "depth" : 5 * mm});
        }
    });
